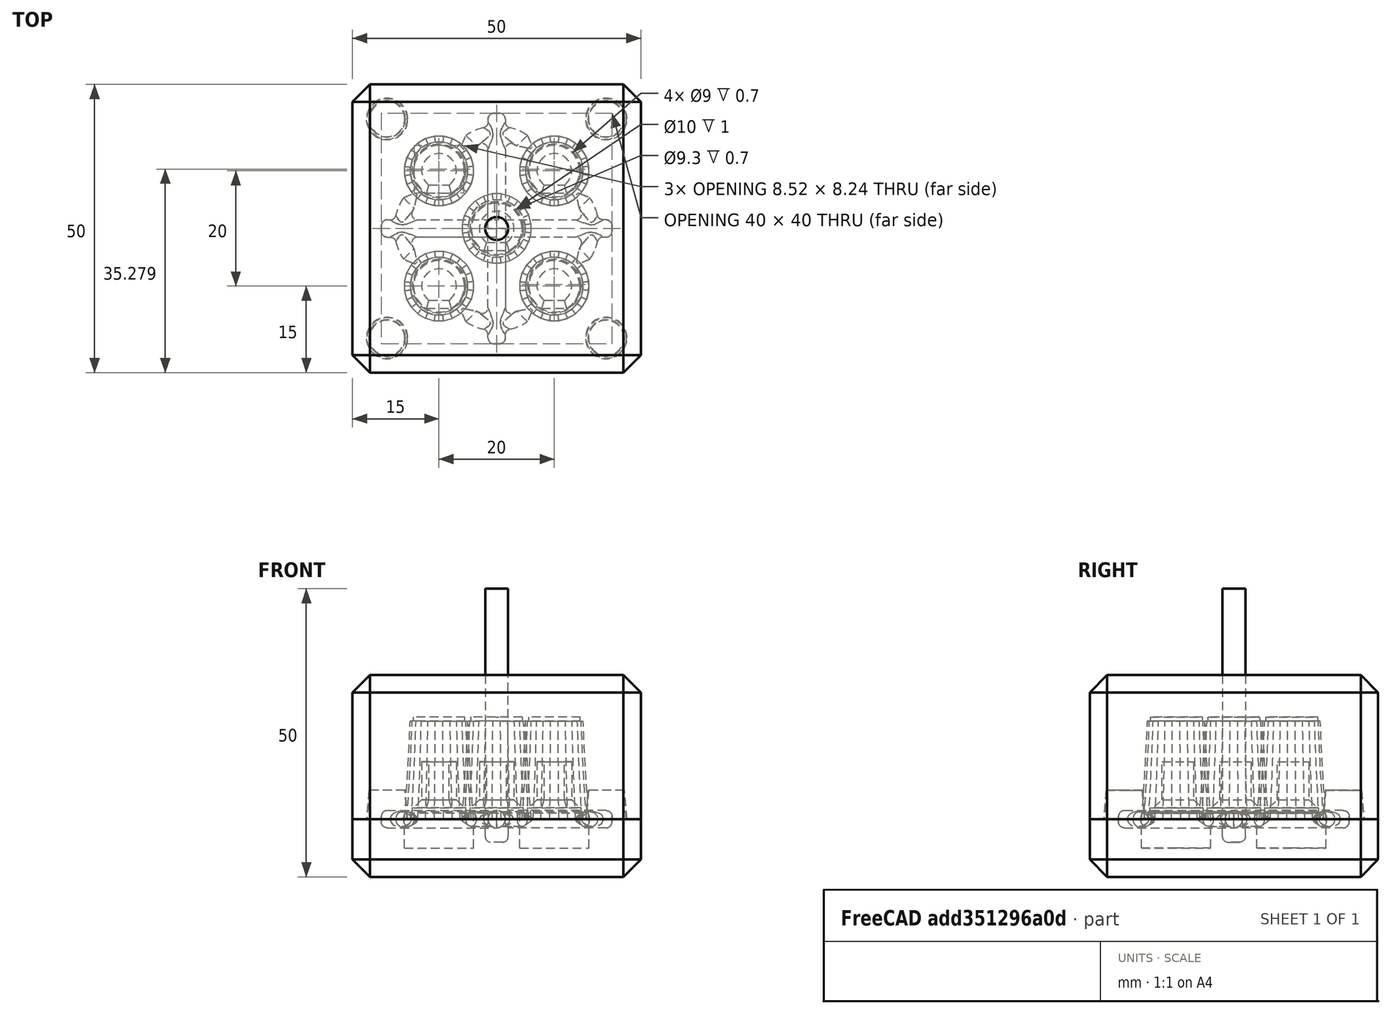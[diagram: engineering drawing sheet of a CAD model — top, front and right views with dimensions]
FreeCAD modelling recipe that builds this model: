
FCSTD DOCUMENT  (FreeCAD 0.19R23141 (Git))
Label: CapMould
License: All rights reserved
LicenseURL: http://en.wikipedia.org/wiki/All_rights_reserved
objects: Sketcher::SketchObject×45, PartDesign::Body×18, PartDesign::Pad×12, PartDesign::FeatureBase×7, PartDesign::Chamfer×6, PartDesign::Boolean×6, PartDesign::AdditiveLoft×5, PartDesign::Pocket×4, PartDesign::Fillet×3, PartDesign::Draft×2, PartDesign::AdditivePipe×1, PartDesign::Revolution×1
note: 144 computed .brp shape members not serialized (recipe doc carries the construction recipe); baked Part::Feature solids carry a one-line shape summary decoded from their .brp

FEATURE [Sketcher::SketchObject] Sketch
  MapMode = 5
  Support = -> [XY_Plane]
  sketch-geometry (25):
    g0: LineSegment StartX=-0.789915 StartY=6 StartZ=0 EndX=-2.31591 EndY=5.59111 EndZ=0
    g1: LineSegment StartX=-2.31591 StartY=5.59111 StartZ=0 EndX=-3.68409 EndY=4.80119 EndZ=0
    g2: LineSegment StartX=-3.68409 StartY=4.80119 StartZ=0 EndX=-4.80119 EndY=3.68409 EndZ=0
    g3: LineSegment StartX=-4.80119 StartY=3.68409 StartZ=0 EndX=-5.59111 EndY=2.31591 EndZ=0
    g4: LineSegment StartX=-5.59111 StartY=2.31591 StartZ=0 EndX=-6 EndY=0.789915 EndZ=0
    g5: LineSegment StartX=-6 StartY=0.789915 StartZ=0 EndX=-6 EndY=-0.789915 EndZ=0
    g6: LineSegment StartX=-6 StartY=-0.789915 StartZ=0 EndX=-5.59111 EndY=-2.31591 EndZ=0
    g7: LineSegment StartX=-5.59111 StartY=-2.31591 StartZ=0 EndX=-4.80119 EndY=-3.68409 EndZ=0
    g8: LineSegment StartX=-4.80119 StartY=-3.68409 StartZ=0 EndX=-3.68409 EndY=-4.80119 EndZ=0
    g9: LineSegment StartX=-3.68409 StartY=-4.80119 StartZ=0 EndX=-2.31591 EndY=-5.59111 EndZ=0
    g10: LineSegment StartX=-2.31591 StartY=-5.59111 StartZ=0 EndX=-0.789915 EndY=-6 EndZ=0
    g11: LineSegment StartX=-0.789915 StartY=-6 StartZ=0 EndX=0.789915 EndY=-6 EndZ=0
    g12: LineSegment StartX=0.789915 StartY=-6 StartZ=0 EndX=2.31591 EndY=-5.59111 EndZ=0
    g13: LineSegment StartX=2.31591 StartY=-5.59111 StartZ=0 EndX=3.68409 EndY=-4.80119 EndZ=0
    g14: LineSegment StartX=3.68409 StartY=-4.80119 StartZ=0 EndX=4.80119 EndY=-3.68409 EndZ=0
    g15: LineSegment StartX=4.80119 StartY=-3.68409 StartZ=0 EndX=5.59111 EndY=-2.31591 EndZ=0
    g16: LineSegment StartX=5.59111 StartY=-2.31591 StartZ=0 EndX=6 EndY=-0.789915 EndZ=0
    g17: LineSegment StartX=6 StartY=-0.789915 StartZ=0 EndX=6 EndY=0.789915 EndZ=0
    g18: LineSegment StartX=6 StartY=0.789915 StartZ=0 EndX=5.59111 EndY=2.31591 EndZ=0
    g19: LineSegment StartX=5.59111 StartY=2.31591 StartZ=0 EndX=4.80119 EndY=3.68409 EndZ=0
    g20: LineSegment StartX=4.80119 StartY=3.68409 StartZ=0 EndX=3.68409 EndY=4.80119 EndZ=0
    g21: LineSegment StartX=3.68409 StartY=4.80119 StartZ=0 EndX=2.31591 EndY=5.59111 EndZ=0
    g22: LineSegment StartX=2.31591 StartY=5.59111 StartZ=0 EndX=0.789915 EndY=6 EndZ=0
    g23: LineSegment StartX=0.789915 StartY=6 StartZ=0 EndX=-0.789915 EndY=6 EndZ=0
    g24: Circle [constr] CenterX=0 CenterY=0 CenterZ=0 NormalX=0 NormalY=0 NormalZ=1 AngleXU=0 Radius=6.05177
  constraints (52):
    c: Coincident(g0,g1)
    c: Coincident(g1,g2)
    c: Coincident(g2,g3)
    c: Coincident(g3,g4)
    c: Coincident(g4,g5)
    c: Coincident(g5,g6)
    c: Coincident(g6,g7)
    c: Coincident(g7,g8)
    c: Coincident(g8,g9)
    c: Coincident(g9,g10)
    c: Coincident(g10,g11)
    c: Coincident(g11,g12)
    c: Coincident(g12,g13)
    c: Coincident(g13,g14)
    c: Coincident(g14,g15)
    c: Coincident(g15,g16)
    c: Coincident(g16,g17)
    c: Coincident(g17,g18)
    c: Coincident(g18,g19)
    c: Coincident(g19,g20)
    c: Coincident(g20,g21)
    c: Coincident(g21,g22)
    c: Coincident(g22,g23)
    c: Coincident(g23,g0)
    c: Equal(g0, g1-g23) x23
    c: PointOnObject(g0,g24)
    c: PointOnObject(g1,g24)
    c: PointOnObject(g2,g24)
    c: PointOnObject(g3,g24)
    c: PointOnObject(g4,g24)
    c: PointOnObject(g5,g24)
    c: PointOnObject(g6,g24)
    c: PointOnObject(g7,g24)
    c: PointOnObject(g8,g24)
    c: PointOnObject(g9,g24)
    c: PointOnObject(g10,g24)
    c: PointOnObject(g11,g24)
    c: PointOnObject(g12,g24)
    c: PointOnObject(g13,g24)
    c: PointOnObject(g14,g24)
    c: PointOnObject(g15,g24)
    c: PointOnObject(g16,g24)
    c: PointOnObject(g17,g24)
    c: PointOnObject(g18,g24)
    c: PointOnObject(g19,g24)
    c: PointOnObject(g20,g24)
    c: PointOnObject(g21,g24)
    c: PointOnObject(g22,g24)
    c: PointOnObject(g23,g24)
    c: Coincident(g24,g-1)
    c: Horizontal(g23)
    c: DistanceX(g4,g17) = 12
FEATURE [Sketcher::SketchObject] Sketch001
  AttachmentOffset = pos=(0,0,7) rot=(0,0,1;0rad)
  MapMode = 5
  Placement = pos=(0,0,7) rot=(0,0,1;0rad)
  Support = -> [XY_Plane]
  sketch-geometry (25):
    g0: LineSegment StartX=-0.724089 StartY=5.5 StartZ=0 EndX=-2.12292 EndY=5.12518 EndZ=0
    g1: LineSegment StartX=-2.12292 StartY=5.12518 StartZ=0 EndX=-3.37708 EndY=4.4011 EndZ=0
    g2: LineSegment StartX=-3.37708 StartY=4.4011 StartZ=0 EndX=-4.4011 EndY=3.37708 EndZ=0
    g3: LineSegment StartX=-4.4011 StartY=3.37708 StartZ=0 EndX=-5.12518 EndY=2.12292 EndZ=0
    g4: LineSegment StartX=-5.12518 StartY=2.12292 StartZ=0 EndX=-5.5 EndY=0.724089 EndZ=0
    g5: LineSegment StartX=-5.5 StartY=0.724089 StartZ=0 EndX=-5.5 EndY=-0.724089 EndZ=0
    g6: LineSegment StartX=-5.5 StartY=-0.724089 StartZ=0 EndX=-5.12518 EndY=-2.12292 EndZ=0
    g7: LineSegment StartX=-5.12518 StartY=-2.12292 StartZ=0 EndX=-4.4011 EndY=-3.37708 EndZ=0
    g8: LineSegment StartX=-4.4011 StartY=-3.37708 StartZ=0 EndX=-3.37708 EndY=-4.4011 EndZ=0
    g9: LineSegment StartX=-3.37708 StartY=-4.4011 StartZ=0 EndX=-2.12292 EndY=-5.12518 EndZ=0
    g10: LineSegment StartX=-2.12292 StartY=-5.12518 StartZ=0 EndX=-0.724089 EndY=-5.5 EndZ=0
    g11: LineSegment StartX=-0.724089 StartY=-5.5 StartZ=0 EndX=0.724089 EndY=-5.5 EndZ=0
    g12: LineSegment StartX=0.724089 StartY=-5.5 StartZ=0 EndX=2.12292 EndY=-5.12518 EndZ=0
    g13: LineSegment StartX=2.12292 StartY=-5.12518 StartZ=0 EndX=3.37708 EndY=-4.4011 EndZ=0
    g14: LineSegment StartX=3.37708 StartY=-4.4011 StartZ=0 EndX=4.4011 EndY=-3.37708 EndZ=0
    g15: LineSegment StartX=4.4011 StartY=-3.37708 StartZ=0 EndX=5.12518 EndY=-2.12292 EndZ=0
    g16: LineSegment StartX=5.12518 StartY=-2.12292 StartZ=0 EndX=5.5 EndY=-0.724089 EndZ=0
    g17: LineSegment StartX=5.5 StartY=-0.724089 StartZ=0 EndX=5.5 EndY=0.724089 EndZ=0
    g18: LineSegment StartX=5.5 StartY=0.724089 StartZ=0 EndX=5.12518 EndY=2.12292 EndZ=0
    g19: LineSegment StartX=5.12518 StartY=2.12292 StartZ=0 EndX=4.4011 EndY=3.37708 EndZ=0
    g20: LineSegment StartX=4.4011 StartY=3.37708 StartZ=0 EndX=3.37708 EndY=4.4011 EndZ=0
    g21: LineSegment StartX=3.37708 StartY=4.4011 StartZ=0 EndX=2.12292 EndY=5.12518 EndZ=0
    g22: LineSegment StartX=2.12292 StartY=5.12518 StartZ=0 EndX=0.724089 EndY=5.5 EndZ=0
    g23: LineSegment StartX=0.724089 StartY=5.5 StartZ=0 EndX=-0.724089 EndY=5.5 EndZ=0
    g24: Circle [constr] CenterX=0 CenterY=0 CenterZ=0 NormalX=0 NormalY=0 NormalZ=1 AngleXU=0 Radius=5.54746
  constraints (52):
    c: Coincident(g0,g1)
    c: Coincident(g1,g2)
    c: Coincident(g2,g3)
    c: Coincident(g3,g4)
    c: Coincident(g4,g5)
    c: Coincident(g5,g6)
    c: Coincident(g6,g7)
    c: Coincident(g7,g8)
    c: Coincident(g8,g9)
    c: Coincident(g9,g10)
    c: Coincident(g10,g11)
    c: Coincident(g11,g12)
    c: Coincident(g12,g13)
    c: Coincident(g13,g14)
    c: Coincident(g14,g15)
    c: Coincident(g15,g16)
    c: Coincident(g16,g17)
    c: Coincident(g17,g18)
    c: Coincident(g18,g19)
    c: Coincident(g19,g20)
    c: Coincident(g20,g21)
    c: Coincident(g21,g22)
    c: Coincident(g22,g23)
    c: Coincident(g23,g0)
    c: Equal(g0, g1-g23) x23
    c: PointOnObject(g0,g24)
    c: PointOnObject(g1,g24)
    c: PointOnObject(g2,g24)
    c: PointOnObject(g3,g24)
    c: PointOnObject(g4,g24)
    c: PointOnObject(g5,g24)
    c: PointOnObject(g6,g24)
    c: PointOnObject(g7,g24)
    c: PointOnObject(g8,g24)
    c: PointOnObject(g9,g24)
    c: PointOnObject(g10,g24)
    c: PointOnObject(g11,g24)
    c: PointOnObject(g12,g24)
    c: PointOnObject(g13,g24)
    c: PointOnObject(g14,g24)
    c: PointOnObject(g15,g24)
    c: PointOnObject(g16,g24)
    c: PointOnObject(g17,g24)
    c: PointOnObject(g18,g24)
    c: PointOnObject(g19,g24)
    c: PointOnObject(g20,g24)
    c: PointOnObject(g21,g24)
    c: PointOnObject(g22,g24)
    c: PointOnObject(g23,g24)
    c: Coincident(g24,g-1)
    c: Horizontal(g23)
    c: DistanceX(g4,g17) = 11
FEATURE [Sketcher::SketchObject] Sketch002
  AttachmentOffset = pos=(0,0,17) rot=(0,0,1;0rad)
  MapMode = 5
  Placement = pos=(0,0,17) rot=(0,0,1;0rad)
  Support = -> [XY_Plane]
  sketch-geometry (25):
    g0: LineSegment StartX=-4.65926 StartY=1.92993 StartZ=0 EndX=-5 EndY=0.658262 EndZ=0
    g1: LineSegment StartX=-5 StartY=0.658262 StartZ=0 EndX=-5 EndY=-0.658262 EndZ=0
    g2: LineSegment StartX=-5 StartY=-0.658262 StartZ=0 EndX=-4.65926 EndY=-1.92993 EndZ=0
    g3: LineSegment StartX=-4.65926 StartY=-1.92993 StartZ=0 EndX=-4.001 EndY=-3.07007 EndZ=0
    g4: LineSegment StartX=-4.001 StartY=-3.07007 StartZ=0 EndX=-3.07007 EndY=-4.001 EndZ=0
    g5: LineSegment StartX=-3.07007 StartY=-4.001 StartZ=0 EndX=-1.92993 EndY=-4.65926 EndZ=0
    g6: LineSegment StartX=-1.92993 StartY=-4.65926 StartZ=0 EndX=-0.658262 EndY=-5 EndZ=0
    g7: LineSegment StartX=-0.658262 StartY=-5 StartZ=0 EndX=0.658262 EndY=-5 EndZ=0
    g8: LineSegment StartX=0.658262 StartY=-5 StartZ=0 EndX=1.92993 EndY=-4.65926 EndZ=0
    g9: LineSegment StartX=1.92993 StartY=-4.65926 StartZ=0 EndX=3.07007 EndY=-4.001 EndZ=0
    g10: LineSegment StartX=3.07007 StartY=-4.001 StartZ=0 EndX=4.001 EndY=-3.07007 EndZ=0
    g11: LineSegment StartX=4.001 StartY=-3.07007 StartZ=0 EndX=4.65926 EndY=-1.92993 EndZ=0
    g12: LineSegment StartX=4.65926 StartY=-1.92993 StartZ=0 EndX=5 EndY=-0.658262 EndZ=0
    g13: LineSegment StartX=5 StartY=-0.658262 StartZ=0 EndX=5 EndY=0.658262 EndZ=0
    g14: LineSegment StartX=5 StartY=0.658262 StartZ=0 EndX=4.65926 EndY=1.92993 EndZ=0
    g15: LineSegment StartX=4.65926 StartY=1.92993 StartZ=0 EndX=4.001 EndY=3.07007 EndZ=0
    g16: LineSegment StartX=4.001 StartY=3.07007 StartZ=0 EndX=3.07007 EndY=4.001 EndZ=0
    g17: LineSegment StartX=3.07007 StartY=4.001 StartZ=0 EndX=1.92993 EndY=4.65926 EndZ=0
    g18: LineSegment StartX=1.92993 StartY=4.65926 StartZ=0 EndX=0.658262 EndY=5 EndZ=0
    g19: LineSegment StartX=0.658262 StartY=5 StartZ=0 EndX=-0.658262 EndY=5 EndZ=0
    g20: LineSegment StartX=-0.658262 StartY=5 StartZ=0 EndX=-1.92993 EndY=4.65926 EndZ=0
    g21: LineSegment StartX=-1.92993 StartY=4.65926 StartZ=0 EndX=-3.07007 EndY=4.001 EndZ=0
    g22: LineSegment StartX=-3.07007 StartY=4.001 StartZ=0 EndX=-4.001 EndY=3.07007 EndZ=0
    g23: LineSegment StartX=-4.001 StartY=3.07007 StartZ=0 EndX=-4.65926 EndY=1.92993 EndZ=0
    g24: Circle [constr] CenterX=0 CenterY=0 CenterZ=0 NormalX=0 NormalY=0 NormalZ=1 AngleXU=0 Radius=5.04314
  constraints (52):
    c: Coincident(g0,g1)
    c: Coincident(g1,g2)
    c: Coincident(g2,g3)
    c: Coincident(g3,g4)
    c: Coincident(g4,g5)
    c: Coincident(g5,g6)
    c: Coincident(g6,g7)
    c: Coincident(g7,g8)
    c: Coincident(g8,g9)
    c: Coincident(g9,g10)
    c: Coincident(g10,g11)
    c: Coincident(g11,g12)
    c: Coincident(g12,g13)
    c: Coincident(g13,g14)
    c: Coincident(g14,g15)
    c: Coincident(g15,g16)
    c: Coincident(g16,g17)
    c: Coincident(g17,g18)
    c: Coincident(g18,g19)
    c: Coincident(g19,g20)
    c: Coincident(g20,g21)
    c: Coincident(g21,g22)
    c: Coincident(g22,g23)
    c: Coincident(g23,g0)
    c: Equal(g0, g1-g23) x23
    c: PointOnObject(g0,g24)
    c: PointOnObject(g1,g24)
    c: PointOnObject(g2,g24)
    c: PointOnObject(g3,g24)
    c: PointOnObject(g4,g24)
    c: PointOnObject(g5,g24)
    c: PointOnObject(g6,g24)
    c: PointOnObject(g7,g24)
    c: PointOnObject(g8,g24)
    c: PointOnObject(g9,g24)
    c: PointOnObject(g10,g24)
    c: PointOnObject(g11,g24)
    c: PointOnObject(g12,g24)
    c: PointOnObject(g13,g24)
    c: PointOnObject(g14,g24)
    c: PointOnObject(g15,g24)
    c: PointOnObject(g16,g24)
    c: PointOnObject(g17,g24)
    c: PointOnObject(g18,g24)
    c: PointOnObject(g19,g24)
    c: PointOnObject(g20,g24)
    c: PointOnObject(g21,g24)
    c: PointOnObject(g22,g24)
    c: PointOnObject(g23,g24)
    c: Coincident(g24,g-1)
    c: Horizontal(g19)
    c: DistanceX(g0,g13) = 10
FEATURE [PartDesign::AdditiveLoft] AdditiveLoft
  AllowMultiFace = false
  Closed = false
  Profile = -> Sketch
  Refine = true
  Ruled = false
  Sections = -> [Sketch001,Sketch002]
FEATURE [Sketcher::SketchObject] Sketch003
  MapMode = 5
  Placement = pos=(0,0,17) rot=(0,0,1;0rad)
  Support = -> [AdditiveLoft]
  sketch-geometry (1):
    g0: Circle CenterX=0 CenterY=0 CenterZ=0 NormalX=0 NormalY=0 NormalZ=1 AngleXU=0 Radius=4.5
  constraints (2):
    c: Coincident(g0,g-1)
    c: Radius(g0) = 4.5
FEATURE [PartDesign::Pad] Pad
  AllowMultiFace = false
  BaseFeature = -> AdditiveLoft
  Direction = (1,1,1)
  Length = 0.7
  Length2 = 100
  Profile = -> Sketch003
  Refine = true
  Type = 0
FEATURE [Sketcher::SketchObject] Sketch004
  AttachmentOffset = pos=(0,0,17.7) rot=(0,0,1;0rad)
  MapMode = 5
  Placement = pos=(0,0,17.7) rot=(0,0,1;0rad)
  Support = -> [XY_Plane001]
  sketch-geometry (10):
    g0: LineSegment StartX=-0.2 StartY=1.5 StartZ=0 EndX=0.2 EndY=1.5 EndZ=0
    g1: LineSegment StartX=0.4 StartY=1.7 StartZ=0 EndX=0.4 EndY=4.2 EndZ=0
    g2: LineSegment StartX=0.2 StartY=4.4 StartZ=0 EndX=-0.2 EndY=4.4 EndZ=0
    g3: LineSegment StartX=-0.4 StartY=4.2 StartZ=0 EndX=-0.4 EndY=1.7 EndZ=0
    g4: ArcOfCircle CenterX=-0.2 CenterY=1.7 CenterZ=0 NormalX=0 NormalY=0 NormalZ=1 AngleXU=0 Radius=0.2 StartAngle=3.14159 EndAngle=4.71239
    g5: ArcOfCircle CenterX=0.2 CenterY=1.7 CenterZ=0 NormalX=0 NormalY=0 NormalZ=1 AngleXU=0 Radius=0.2 StartAngle=4.71239 EndAngle=6.28319
    g6: ArcOfCircle CenterX=0.2 CenterY=4.2 CenterZ=0 NormalX=0 NormalY=0 NormalZ=1 AngleXU=0 Radius=0.2 StartAngle=1.4e-15 EndAngle=1.5708
    g7: ArcOfCircle CenterX=-0.2 CenterY=4.2 CenterZ=0 NormalX=0 NormalY=0 NormalZ=1 AngleXU=0 Radius=0.2 StartAngle=1.5708 EndAngle=3.14159
    g8: LineSegment [constr] StartX=-0.2 StartY=1.7 StartZ=0 EndX=0 EndY=0 EndZ=0
    g9: LineSegment [constr] StartX=0 StartY=0 StartZ=0 EndX=0.2 EndY=1.7 EndZ=0
  constraints (24):
    c: Horizontal(g0)
    c: Horizontal(g2)
    c: Vertical(g1)
    c: Vertical(g3)
    c: Tangent(g3,g4) = -1.5708
    c: Tangent(g0,g4) = -1.5708
    c: Tangent(g0,g5) = -1.5708
    c: Tangent(g1,g5) = -1.5708
    c: Tangent(g1,g6) = -1.5708
    c: Tangent(g2,g6) = -1.5708
    c: Tangent(g2,g7) = -1.5708
    c: Tangent(g3,g7) = -1.5708
    c: Radius(g7) = 0.2
    c: Equal(g7,g6)
    c: Equal(g7,g5)
    c: Equal(g7,g4)
    c: Coincident(g8,g4)
    c: Coincident(g8,g-1)
    c: Coincident(g9,g-1)
    c: Coincident(g9,g5)
    c: Equal(g9,g8)
    c: DistanceX(g3,g1) = 0.8
    c: DistanceY(g-1,g2) = 4.4
    c: DistanceY(g-1,g0) = 1.5
FEATURE [PartDesign::Pad] Pad001
  AllowMultiFace = false
  Direction = (1,1,1)
  Length = 0.02
  Length2 = 100
  Profile = -> Sketch004
  Refine = true
  Type = 0
FEATURE [PartDesign::Body] Body001  label="Indicator"
  Group = -> [Sketch004,Pad001]
  Origin = -> Origin001
  Tip = -> Pad001
FEATURE [Sketcher::SketchObject] Sketch005
  MapMode = 5
  Placement = pos=(0,0,0) rot=(1,0,0;3.14159rad)
  Support = -> [Pad]
  sketch-geometry (1):
    g0: Circle CenterX=0 CenterY=0 CenterZ=0 NormalX=0 NormalY=0 NormalZ=1 AngleXU=0 Radius=5
  constraints (2):
    c: Coincident(g0,g-1)
    c: Radius(g0) = 5
FEATURE [Sketcher::SketchObject] Sketch006
  MapMode = 5
  Placement = pos=(0,0,1) rot=(1,0,0;3.14159rad)
  sketch-geometry (1):
    g0: Circle CenterX=0 CenterY=0 CenterZ=0 NormalX=0 NormalY=0 NormalZ=1 AngleXU=0 Radius=4.65
  constraints (2):
    c: Coincident(g0,g-1)
    c: Radius(g0) = 4.65
FEATURE [Sketcher::SketchObject] Sketch007
  MapMode = 5
  Placement = pos=(0,0,2) rot=(1,0,0;3.14159rad)
  sketch-geometry (2):
    g0: ArcOfCircle CenterX=0 CenterY=0 CenterZ=0 NormalX=0 NormalY=0 NormalZ=1 AngleXU=0 Radius=3 StartAngle=2.19024 EndAngle=7.23453
    g1: LineSegment StartX=-1.74176 StartY=2.4426 StartZ=0 EndX=1.74176 EndY=2.4426 EndZ=0
  constraints (5):
    c: Coincident(g0,g-1)
    c: Coincident(g1,g0)
    c: Coincident(g1,g0)
    c: Horizontal(g1)
    c: Radius(g0) = 3
FEATURE [PartDesign::Body] Body  label="Outer"
  Group = -> [Sketch,Sketch001,Sketch002,AdditiveLoft,Sketch003,Pad,Sketch005,Sketch006,Sketch007]
  Origin = -> Origin
  Placement = pos=(-10,-10,0) rot=(0,0,1;0rad)
  Tip = -> Pad
FEATURE [Sketcher::SketchObject] Sketch008
  MapMode = 5
  Support = -> [XY_Plane002]
  sketch-geometry (5):
    g0: LineSegment StartX=-25 StartY=25 StartZ=0 EndX=-25 EndY=-25 EndZ=0
    g1: LineSegment StartX=-25 StartY=-25 StartZ=0 EndX=25 EndY=-25 EndZ=0
    g2: LineSegment StartX=25 StartY=-25 StartZ=0 EndX=25 EndY=25 EndZ=0
    g3: LineSegment StartX=25 StartY=25 StartZ=0 EndX=-25 EndY=25 EndZ=0
    g4: Circle [constr] CenterX=0 CenterY=0 CenterZ=0 NormalX=0 NormalY=0 NormalZ=1 AngleXU=0 Radius=35.3553
  constraints (14):
    c: Coincident(g0,g1)
    c: Coincident(g1,g2)
    c: Coincident(g2,g3)
    c: Coincident(g3,g0)
    c: Equal(g0,g1)
    c: Equal(g0,g2)
    c: Equal(g0,g3)
    c: PointOnObject(g0,g4)
    c: PointOnObject(g1,g4)
    c: PointOnObject(g2,g4)
    c: PointOnObject(g3,g4)
    c: Coincident(g4,g-1)
    c: Horizontal(g3)
    c: DistanceX(g3,g3) = 50
FEATURE [PartDesign::Pad] Pad002
  Direction = (1,1,1)
  Length = 25
  Length2 = 100
  Profile = -> Sketch008
  Type = 0
FEATURE [Sketcher::SketchObject] Sketch009
  AttachmentOffset = pos=(0,0,17) rot=(0,0,1;0rad)
  MapMode = 5
  Placement = pos=(0,0,17) rot=(0,0,1;0rad)
  Support = -> [XY_Plane003]
  sketch-geometry (25):
    g0: LineSegment StartX=-4.65926 StartY=1.92993 StartZ=0 EndX=-5 EndY=0.658262 EndZ=0
    g1: LineSegment StartX=-5 StartY=0.658262 StartZ=0 EndX=-5 EndY=-0.658262 EndZ=0
    g2: LineSegment StartX=-5 StartY=-0.658262 StartZ=0 EndX=-4.65926 EndY=-1.92993 EndZ=0
    g3: LineSegment StartX=-4.65926 StartY=-1.92993 StartZ=0 EndX=-4.001 EndY=-3.07007 EndZ=0
    g4: LineSegment StartX=-4.001 StartY=-3.07007 StartZ=0 EndX=-3.07007 EndY=-4.001 EndZ=0
    g5: LineSegment StartX=-3.07007 StartY=-4.001 StartZ=0 EndX=-1.92993 EndY=-4.65926 EndZ=0
    g6: LineSegment StartX=-1.92993 StartY=-4.65926 StartZ=0 EndX=-0.658262 EndY=-5 EndZ=0
    g7: LineSegment StartX=-0.658262 StartY=-5 StartZ=0 EndX=0.658262 EndY=-5 EndZ=0
    g8: LineSegment StartX=0.658262 StartY=-5 StartZ=0 EndX=1.92993 EndY=-4.65926 EndZ=0
    g9: LineSegment StartX=1.92993 StartY=-4.65926 StartZ=0 EndX=3.07007 EndY=-4.001 EndZ=0
    g10: LineSegment StartX=3.07007 StartY=-4.001 StartZ=0 EndX=4.001 EndY=-3.07007 EndZ=0
    g11: LineSegment StartX=4.001 StartY=-3.07007 StartZ=0 EndX=4.65926 EndY=-1.92993 EndZ=0
    g12: LineSegment StartX=4.65926 StartY=-1.92993 StartZ=0 EndX=5 EndY=-0.658262 EndZ=0
    g13: LineSegment StartX=5 StartY=-0.658262 StartZ=0 EndX=5 EndY=0.658262 EndZ=0
    g14: LineSegment StartX=5 StartY=0.658262 StartZ=0 EndX=4.65926 EndY=1.92993 EndZ=0
    g15: LineSegment StartX=4.65926 StartY=1.92993 StartZ=0 EndX=4.001 EndY=3.07007 EndZ=0
    g16: LineSegment StartX=4.001 StartY=3.07007 StartZ=0 EndX=3.07007 EndY=4.001 EndZ=0
    g17: LineSegment StartX=3.07007 StartY=4.001 StartZ=0 EndX=1.92993 EndY=4.65926 EndZ=0
    g18: LineSegment StartX=1.92993 StartY=4.65926 StartZ=0 EndX=0.658262 EndY=5 EndZ=0
    g19: LineSegment StartX=0.658262 StartY=5 StartZ=0 EndX=-0.658262 EndY=5 EndZ=0
    g20: LineSegment StartX=-0.658262 StartY=5 StartZ=0 EndX=-1.92993 EndY=4.65926 EndZ=0
    g21: LineSegment StartX=-1.92993 StartY=4.65926 StartZ=0 EndX=-3.07007 EndY=4.001 EndZ=0
    g22: LineSegment StartX=-3.07007 StartY=4.001 StartZ=0 EndX=-4.001 EndY=3.07007 EndZ=0
    g23: LineSegment StartX=-4.001 StartY=3.07007 StartZ=0 EndX=-4.65926 EndY=1.92993 EndZ=0
    g24: Circle [constr] CenterX=0 CenterY=0 CenterZ=0 NormalX=0 NormalY=0 NormalZ=1 AngleXU=0 Radius=5.04314
  constraints (52):
    c: Coincident(g0,g1)
    c: Coincident(g1,g2)
    c: Coincident(g2,g3)
    c: Coincident(g3,g4)
    c: Coincident(g4,g5)
    c: Coincident(g5,g6)
    c: Coincident(g6,g7)
    c: Coincident(g7,g8)
    c: Coincident(g8,g9)
    c: Coincident(g9,g10)
    c: Coincident(g10,g11)
    c: Coincident(g11,g12)
    c: Coincident(g12,g13)
    c: Coincident(g13,g14)
    c: Coincident(g14,g15)
    c: Coincident(g15,g16)
    c: Coincident(g16,g17)
    c: Coincident(g17,g18)
    c: Coincident(g18,g19)
    c: Coincident(g19,g20)
    c: Coincident(g20,g21)
    c: Coincident(g21,g22)
    c: Coincident(g22,g23)
    c: Coincident(g23,g0)
    c: Equal(g0, g1-g23) x23
    c: PointOnObject(g0,g24)
    c: PointOnObject(g1,g24)
    c: PointOnObject(g2,g24)
    c: PointOnObject(g3,g24)
    c: PointOnObject(g4,g24)
    c: PointOnObject(g5,g24)
    c: PointOnObject(g6,g24)
    c: PointOnObject(g7,g24)
    c: PointOnObject(g8,g24)
    c: PointOnObject(g9,g24)
    c: PointOnObject(g10,g24)
    c: PointOnObject(g11,g24)
    c: PointOnObject(g12,g24)
    c: PointOnObject(g13,g24)
    c: PointOnObject(g14,g24)
    c: PointOnObject(g15,g24)
    c: PointOnObject(g16,g24)
    c: PointOnObject(g17,g24)
    c: PointOnObject(g18,g24)
    c: PointOnObject(g19,g24)
    c: PointOnObject(g20,g24)
    c: PointOnObject(g21,g24)
    c: PointOnObject(g22,g24)
    c: PointOnObject(g23,g24)
    c: Coincident(g24,g-1)
    c: Horizontal(g19)
    c: DistanceX(g0,g13) = 10
FEATURE [Sketcher::SketchObject] Sketch011
  MapMode = 5
  Support = -> [XY_Plane003]
  sketch-geometry (25):
    g0: LineSegment StartX=-0.789915 StartY=6 StartZ=0 EndX=-2.31591 EndY=5.59111 EndZ=0
    g1: LineSegment StartX=-2.31591 StartY=5.59111 StartZ=0 EndX=-3.68409 EndY=4.80119 EndZ=0
    g2: LineSegment StartX=-3.68409 StartY=4.80119 StartZ=0 EndX=-4.80119 EndY=3.68409 EndZ=0
    g3: LineSegment StartX=-4.80119 StartY=3.68409 StartZ=0 EndX=-5.59111 EndY=2.31591 EndZ=0
    g4: LineSegment StartX=-5.59111 StartY=2.31591 StartZ=0 EndX=-6 EndY=0.789915 EndZ=0
    g5: LineSegment StartX=-6 StartY=0.789915 StartZ=0 EndX=-6 EndY=-0.789915 EndZ=0
    g6: LineSegment StartX=-6 StartY=-0.789915 StartZ=0 EndX=-5.59111 EndY=-2.31591 EndZ=0
    g7: LineSegment StartX=-5.59111 StartY=-2.31591 StartZ=0 EndX=-4.80119 EndY=-3.68409 EndZ=0
    g8: LineSegment StartX=-4.80119 StartY=-3.68409 StartZ=0 EndX=-3.68409 EndY=-4.80119 EndZ=0
    g9: LineSegment StartX=-3.68409 StartY=-4.80119 StartZ=0 EndX=-2.31591 EndY=-5.59111 EndZ=0
    g10: LineSegment StartX=-2.31591 StartY=-5.59111 StartZ=0 EndX=-0.789915 EndY=-6 EndZ=0
    g11: LineSegment StartX=-0.789915 StartY=-6 StartZ=0 EndX=0.789915 EndY=-6 EndZ=0
    g12: LineSegment StartX=0.789915 StartY=-6 StartZ=0 EndX=2.31591 EndY=-5.59111 EndZ=0
    g13: LineSegment StartX=2.31591 StartY=-5.59111 StartZ=0 EndX=3.68409 EndY=-4.80119 EndZ=0
    g14: LineSegment StartX=3.68409 StartY=-4.80119 StartZ=0 EndX=4.80119 EndY=-3.68409 EndZ=0
    g15: LineSegment StartX=4.80119 StartY=-3.68409 StartZ=0 EndX=5.59111 EndY=-2.31591 EndZ=0
    g16: LineSegment StartX=5.59111 StartY=-2.31591 StartZ=0 EndX=6 EndY=-0.789915 EndZ=0
    g17: LineSegment StartX=6 StartY=-0.789915 StartZ=0 EndX=6 EndY=0.789915 EndZ=0
    g18: LineSegment StartX=6 StartY=0.789915 StartZ=0 EndX=5.59111 EndY=2.31591 EndZ=0
    g19: LineSegment StartX=5.59111 StartY=2.31591 StartZ=0 EndX=4.80119 EndY=3.68409 EndZ=0
    g20: LineSegment StartX=4.80119 StartY=3.68409 StartZ=0 EndX=3.68409 EndY=4.80119 EndZ=0
    g21: LineSegment StartX=3.68409 StartY=4.80119 StartZ=0 EndX=2.31591 EndY=5.59111 EndZ=0
    g22: LineSegment StartX=2.31591 StartY=5.59111 StartZ=0 EndX=0.789915 EndY=6 EndZ=0
    g23: LineSegment StartX=0.789915 StartY=6 StartZ=0 EndX=-0.789915 EndY=6 EndZ=0
    g24: Circle [constr] CenterX=0 CenterY=0 CenterZ=0 NormalX=0 NormalY=0 NormalZ=1 AngleXU=0 Radius=6.05177
  constraints (52):
    c: Coincident(g0,g1)
    c: Coincident(g1,g2)
    c: Coincident(g2,g3)
    c: Coincident(g3,g4)
    c: Coincident(g4,g5)
    c: Coincident(g5,g6)
    c: Coincident(g6,g7)
    c: Coincident(g7,g8)
    c: Coincident(g8,g9)
    c: Coincident(g9,g10)
    c: Coincident(g10,g11)
    c: Coincident(g11,g12)
    c: Coincident(g12,g13)
    c: Coincident(g13,g14)
    c: Coincident(g14,g15)
    c: Coincident(g15,g16)
    c: Coincident(g16,g17)
    c: Coincident(g17,g18)
    c: Coincident(g18,g19)
    c: Coincident(g19,g20)
    c: Coincident(g20,g21)
    c: Coincident(g21,g22)
    c: Coincident(g22,g23)
    c: Coincident(g23,g0)
    c: Equal(g0, g1-g23) x23
    c: PointOnObject(g0,g24)
    c: PointOnObject(g1,g24)
    c: PointOnObject(g2,g24)
    c: PointOnObject(g3,g24)
    c: PointOnObject(g4,g24)
    c: PointOnObject(g5,g24)
    c: PointOnObject(g6,g24)
    c: PointOnObject(g7,g24)
    c: PointOnObject(g8,g24)
    c: PointOnObject(g9,g24)
    c: PointOnObject(g10,g24)
    c: PointOnObject(g11,g24)
    c: PointOnObject(g12,g24)
    c: PointOnObject(g13,g24)
    c: PointOnObject(g14,g24)
    c: PointOnObject(g15,g24)
    c: PointOnObject(g16,g24)
    c: PointOnObject(g17,g24)
    c: PointOnObject(g18,g24)
    c: PointOnObject(g19,g24)
    c: PointOnObject(g20,g24)
    c: PointOnObject(g21,g24)
    c: PointOnObject(g22,g24)
    c: PointOnObject(g23,g24)
    c: Coincident(g24,g-1)
    c: Horizontal(g23)
    c: DistanceX(g4,g17) = 12
FEATURE [Sketcher::SketchObject] Sketch012
  AttachmentOffset = pos=(0,0,7) rot=(0,0,1;0rad)
  MapMode = 5
  Placement = pos=(0,0,7) rot=(0,0,1;0rad)
  Support = -> [XY_Plane003]
  sketch-geometry (25):
    g0: LineSegment StartX=-0.724089 StartY=5.5 StartZ=0 EndX=-2.12292 EndY=5.12518 EndZ=0
    g1: LineSegment StartX=-2.12292 StartY=5.12518 StartZ=0 EndX=-3.37708 EndY=4.4011 EndZ=0
    g2: LineSegment StartX=-3.37708 StartY=4.4011 StartZ=0 EndX=-4.4011 EndY=3.37708 EndZ=0
    g3: LineSegment StartX=-4.4011 StartY=3.37708 StartZ=0 EndX=-5.12518 EndY=2.12292 EndZ=0
    g4: LineSegment StartX=-5.12518 StartY=2.12292 StartZ=0 EndX=-5.5 EndY=0.724089 EndZ=0
    g5: LineSegment StartX=-5.5 StartY=0.724089 StartZ=0 EndX=-5.5 EndY=-0.724089 EndZ=0
    g6: LineSegment StartX=-5.5 StartY=-0.724089 StartZ=0 EndX=-5.12518 EndY=-2.12292 EndZ=0
    g7: LineSegment StartX=-5.12518 StartY=-2.12292 StartZ=0 EndX=-4.4011 EndY=-3.37708 EndZ=0
    g8: LineSegment StartX=-4.4011 StartY=-3.37708 StartZ=0 EndX=-3.37708 EndY=-4.4011 EndZ=0
    g9: LineSegment StartX=-3.37708 StartY=-4.4011 StartZ=0 EndX=-2.12292 EndY=-5.12518 EndZ=0
    g10: LineSegment StartX=-2.12292 StartY=-5.12518 StartZ=0 EndX=-0.724089 EndY=-5.5 EndZ=0
    g11: LineSegment StartX=-0.724089 StartY=-5.5 StartZ=0 EndX=0.724089 EndY=-5.5 EndZ=0
    g12: LineSegment StartX=0.724089 StartY=-5.5 StartZ=0 EndX=2.12292 EndY=-5.12518 EndZ=0
    g13: LineSegment StartX=2.12292 StartY=-5.12518 StartZ=0 EndX=3.37708 EndY=-4.4011 EndZ=0
    g14: LineSegment StartX=3.37708 StartY=-4.4011 StartZ=0 EndX=4.4011 EndY=-3.37708 EndZ=0
    g15: LineSegment StartX=4.4011 StartY=-3.37708 StartZ=0 EndX=5.12518 EndY=-2.12292 EndZ=0
    g16: LineSegment StartX=5.12518 StartY=-2.12292 StartZ=0 EndX=5.5 EndY=-0.724089 EndZ=0
    g17: LineSegment StartX=5.5 StartY=-0.724089 StartZ=0 EndX=5.5 EndY=0.724089 EndZ=0
    g18: LineSegment StartX=5.5 StartY=0.724089 StartZ=0 EndX=5.12518 EndY=2.12292 EndZ=0
    g19: LineSegment StartX=5.12518 StartY=2.12292 StartZ=0 EndX=4.4011 EndY=3.37708 EndZ=0
    g20: LineSegment StartX=4.4011 StartY=3.37708 StartZ=0 EndX=3.37708 EndY=4.4011 EndZ=0
    g21: LineSegment StartX=3.37708 StartY=4.4011 StartZ=0 EndX=2.12292 EndY=5.12518 EndZ=0
    g22: LineSegment StartX=2.12292 StartY=5.12518 StartZ=0 EndX=0.724089 EndY=5.5 EndZ=0
    g23: LineSegment StartX=0.724089 StartY=5.5 StartZ=0 EndX=-0.724089 EndY=5.5 EndZ=0
    g24: Circle [constr] CenterX=0 CenterY=0 CenterZ=0 NormalX=0 NormalY=0 NormalZ=1 AngleXU=0 Radius=5.54746
  constraints (52):
    c: Coincident(g0,g1)
    c: Coincident(g1,g2)
    c: Coincident(g2,g3)
    c: Coincident(g3,g4)
    c: Coincident(g4,g5)
    c: Coincident(g5,g6)
    c: Coincident(g6,g7)
    c: Coincident(g7,g8)
    c: Coincident(g8,g9)
    c: Coincident(g9,g10)
    c: Coincident(g10,g11)
    c: Coincident(g11,g12)
    c: Coincident(g12,g13)
    c: Coincident(g13,g14)
    c: Coincident(g14,g15)
    c: Coincident(g15,g16)
    c: Coincident(g16,g17)
    c: Coincident(g17,g18)
    c: Coincident(g18,g19)
    c: Coincident(g19,g20)
    c: Coincident(g20,g21)
    c: Coincident(g21,g22)
    c: Coincident(g22,g23)
    c: Coincident(g23,g0)
    c: Equal(g0, g1-g23) x23
    c: PointOnObject(g0,g24)
    c: PointOnObject(g1,g24)
    c: PointOnObject(g2,g24)
    c: PointOnObject(g3,g24)
    c: PointOnObject(g4,g24)
    c: PointOnObject(g5,g24)
    c: PointOnObject(g6,g24)
    c: PointOnObject(g7,g24)
    c: PointOnObject(g8,g24)
    c: PointOnObject(g9,g24)
    c: PointOnObject(g10,g24)
    c: PointOnObject(g11,g24)
    c: PointOnObject(g12,g24)
    c: PointOnObject(g13,g24)
    c: PointOnObject(g14,g24)
    c: PointOnObject(g15,g24)
    c: PointOnObject(g16,g24)
    c: PointOnObject(g17,g24)
    c: PointOnObject(g18,g24)
    c: PointOnObject(g19,g24)
    c: PointOnObject(g20,g24)
    c: PointOnObject(g21,g24)
    c: PointOnObject(g22,g24)
    c: PointOnObject(g23,g24)
    c: Coincident(g24,g-1)
    c: Horizontal(g23)
    c: DistanceX(g4,g17) = 11
FEATURE [PartDesign::AdditiveLoft] AdditiveLoft001
  AllowMultiFace = false
  Closed = false
  Profile = -> Sketch011
  Refine = true
  Ruled = false
  Sections = -> [Sketch012,Sketch009]
FEATURE [Sketcher::SketchObject] Sketch010
  MapMode = 5
  Placement = pos=(0,0,17) rot=(0,0,1;0rad)
  Support = -> [AdditiveLoft001]
  sketch-geometry (1):
    g0: Circle CenterX=0 CenterY=0 CenterZ=0 NormalX=0 NormalY=0 NormalZ=1 AngleXU=0 Radius=4.5
  constraints (2):
    c: Coincident(g0,g-1)
    c: Radius(g0) = 4.5
FEATURE [PartDesign::Pad] Pad003
  AllowMultiFace = false
  BaseFeature = -> AdditiveLoft001
  Direction = (1,1,1)
  Length = 0.7
  Length2 = 100
  Profile = -> Sketch010
  Refine = true
  Type = 0
FEATURE [Sketcher::SketchObject] Sketch013
  MapMode = 5
  Placement = pos=(0,0,0) rot=(1,0,0;3.14159rad)
  Support = -> [Pad003]
  sketch-geometry (1):
    g0: Circle CenterX=0 CenterY=0 CenterZ=0 NormalX=0 NormalY=0 NormalZ=1 AngleXU=0 Radius=5
  constraints (2):
    c: Coincident(g0,g-1)
    c: Radius(g0) = 5
FEATURE [PartDesign::Pocket] Pocket003
  AllowMultiFace = false
  BaseFeature = -> Pad003
  Length = 1
  Length2 = 100
  Profile = -> Sketch013
  Refine = true
  Type = 0
FEATURE [Sketcher::SketchObject] Sketch014
  MapMode = 5
  Placement = pos=(0,0,1) rot=(1,0,0;3.14159rad)
  Support = -> [Pocket003]
  sketch-geometry (1):
    g0: Circle CenterX=0 CenterY=0 CenterZ=0 NormalX=0 NormalY=0 NormalZ=1 AngleXU=0 Radius=4.65
  constraints (2):
    c: Coincident(g0,g-1)
    c: Radius(g0) = 4.65
FEATURE [PartDesign::Pocket] Pocket004
  AllowMultiFace = false
  BaseFeature = -> Pocket003
  Length = 1
  Length2 = 100
  Profile = -> Sketch014
  Refine = true
  Type = 0
FEATURE [Sketcher::SketchObject] Sketch015
  MapMode = 5
  Placement = pos=(0,0,2) rot=(1,0,0;3.14159rad)
  Support = -> [Pocket004]
  sketch-geometry (2):
    g0: ArcOfCircle CenterX=0 CenterY=0 CenterZ=0 NormalX=0 NormalY=0 NormalZ=1 AngleXU=0 Radius=3 StartAngle=2.19024 EndAngle=7.23453
    g1: LineSegment StartX=-1.74176 StartY=2.4426 StartZ=0 EndX=1.74176 EndY=2.4426 EndZ=0
  constraints (5):
    c: Coincident(g0,g-1)
    c: Coincident(g1,g0)
    c: Coincident(g1,g0)
    c: Horizontal(g1)
    c: Radius(g0) = 3
FEATURE [PartDesign::Pocket] Pocket005
  AllowMultiFace = false
  BaseFeature = -> Pocket004
  Length = 8
  Length2 = 100
  Profile = -> Sketch015
  Refine = true
  Type = 0
FEATURE [PartDesign::Chamfer] Chamfer002
  Angle = 45
  Base = -> Pocket005 [Edge82,Edge83]
  BaseFeature = -> Pocket005
  ChamferType = 0
  FlipDirection = false
  Size = 1.4
  Size2 = 1
  SupportTransform = false
FEATURE [PartDesign::Chamfer] Chamfer003
  Angle = 45
  Base = -> Chamfer002 [Edge8]
  BaseFeature = -> Chamfer002
  ChamferType = 0
  FlipDirection = false
  Size = 0.3
  Size2 = 1
  SupportTransform = false
FEATURE [PartDesign::Fillet] Fillet001
  Base = -> Chamfer003 [Edge93,Face36]
  BaseFeature = -> Chamfer003
  Radius = 0.1
  SupportTransform = false
FEATURE [PartDesign::Body] Body003  label="Inner"
  Group = -> [Sketch011,Sketch012,Sketch009,AdditiveLoft001,Sketch010,Pad003,Sketch013,Pocket003,Sketch014,Pocket004,Sketch015,Pocket005,Chamfer002,Chamfer003,Fillet001]
  Origin = -> Origin003
  Tip = -> Fillet001
FEATURE [Sketcher::SketchObject] Sketch016
  AttachmentOffset = pos=(0,0,17) rot=(0,0,1;0rad)
  MapMode = 5
  Placement = pos=(0,0,17) rot=(0,0,1;0rad)
  Support = -> [XY_Plane004]
  sketch-geometry (25):
    g0: LineSegment StartX=-4.65926 StartY=1.92993 StartZ=0 EndX=-5 EndY=0.658262 EndZ=0
    g1: LineSegment StartX=-5 StartY=0.658262 StartZ=0 EndX=-5 EndY=-0.658262 EndZ=0
    g2: LineSegment StartX=-5 StartY=-0.658262 StartZ=0 EndX=-4.65926 EndY=-1.92993 EndZ=0
    g3: LineSegment StartX=-4.65926 StartY=-1.92993 StartZ=0 EndX=-4.001 EndY=-3.07007 EndZ=0
    g4: LineSegment StartX=-4.001 StartY=-3.07007 StartZ=0 EndX=-3.07007 EndY=-4.001 EndZ=0
    g5: LineSegment StartX=-3.07007 StartY=-4.001 StartZ=0 EndX=-1.92993 EndY=-4.65926 EndZ=0
    g6: LineSegment StartX=-1.92993 StartY=-4.65926 StartZ=0 EndX=-0.658262 EndY=-5 EndZ=0
    g7: LineSegment StartX=-0.658262 StartY=-5 StartZ=0 EndX=0.658262 EndY=-5 EndZ=0
    g8: LineSegment StartX=0.658262 StartY=-5 StartZ=0 EndX=1.92993 EndY=-4.65926 EndZ=0
    g9: LineSegment StartX=1.92993 StartY=-4.65926 StartZ=0 EndX=3.07007 EndY=-4.001 EndZ=0
    g10: LineSegment StartX=3.07007 StartY=-4.001 StartZ=0 EndX=4.001 EndY=-3.07007 EndZ=0
    g11: LineSegment StartX=4.001 StartY=-3.07007 StartZ=0 EndX=4.65926 EndY=-1.92993 EndZ=0
    g12: LineSegment StartX=4.65926 StartY=-1.92993 StartZ=0 EndX=5 EndY=-0.658262 EndZ=0
    g13: LineSegment StartX=5 StartY=-0.658262 StartZ=0 EndX=5 EndY=0.658262 EndZ=0
    g14: LineSegment StartX=5 StartY=0.658262 StartZ=0 EndX=4.65926 EndY=1.92993 EndZ=0
    g15: LineSegment StartX=4.65926 StartY=1.92993 StartZ=0 EndX=4.001 EndY=3.07007 EndZ=0
    g16: LineSegment StartX=4.001 StartY=3.07007 StartZ=0 EndX=3.07007 EndY=4.001 EndZ=0
    g17: LineSegment StartX=3.07007 StartY=4.001 StartZ=0 EndX=1.92993 EndY=4.65926 EndZ=0
    g18: LineSegment StartX=1.92993 StartY=4.65926 StartZ=0 EndX=0.658262 EndY=5 EndZ=0
    g19: LineSegment StartX=0.658262 StartY=5 StartZ=0 EndX=-0.658262 EndY=5 EndZ=0
    g20: LineSegment StartX=-0.658262 StartY=5 StartZ=0 EndX=-1.92993 EndY=4.65926 EndZ=0
    g21: LineSegment StartX=-1.92993 StartY=4.65926 StartZ=0 EndX=-3.07007 EndY=4.001 EndZ=0
    g22: LineSegment StartX=-3.07007 StartY=4.001 StartZ=0 EndX=-4.001 EndY=3.07007 EndZ=0
    g23: LineSegment StartX=-4.001 StartY=3.07007 StartZ=0 EndX=-4.65926 EndY=1.92993 EndZ=0
    g24: Circle [constr] CenterX=0 CenterY=0 CenterZ=0 NormalX=0 NormalY=0 NormalZ=1 AngleXU=0 Radius=5.04314
  constraints (52):
    c: Coincident(g0,g1)
    c: Coincident(g1,g2)
    c: Coincident(g2,g3)
    c: Coincident(g3,g4)
    c: Coincident(g4,g5)
    c: Coincident(g5,g6)
    c: Coincident(g6,g7)
    c: Coincident(g7,g8)
    c: Coincident(g8,g9)
    c: Coincident(g9,g10)
    c: Coincident(g10,g11)
    c: Coincident(g11,g12)
    c: Coincident(g12,g13)
    c: Coincident(g13,g14)
    c: Coincident(g14,g15)
    c: Coincident(g15,g16)
    c: Coincident(g16,g17)
    c: Coincident(g17,g18)
    c: Coincident(g18,g19)
    c: Coincident(g19,g20)
    c: Coincident(g20,g21)
    c: Coincident(g21,g22)
    c: Coincident(g22,g23)
    c: Coincident(g23,g0)
    c: Equal(g0, g1-g23) x23
    c: PointOnObject(g0,g24)
    c: PointOnObject(g1,g24)
    c: PointOnObject(g2,g24)
    c: PointOnObject(g3,g24)
    c: PointOnObject(g4,g24)
    c: PointOnObject(g5,g24)
    c: PointOnObject(g6,g24)
    c: PointOnObject(g7,g24)
    c: PointOnObject(g8,g24)
    c: PointOnObject(g9,g24)
    c: PointOnObject(g10,g24)
    c: PointOnObject(g11,g24)
    c: PointOnObject(g12,g24)
    c: PointOnObject(g13,g24)
    c: PointOnObject(g14,g24)
    c: PointOnObject(g15,g24)
    c: PointOnObject(g16,g24)
    c: PointOnObject(g17,g24)
    c: PointOnObject(g18,g24)
    c: PointOnObject(g19,g24)
    c: PointOnObject(g20,g24)
    c: PointOnObject(g21,g24)
    c: PointOnObject(g22,g24)
    c: PointOnObject(g23,g24)
    c: Coincident(g24,g-1)
    c: Horizontal(g19)
    c: DistanceX(g0,g13) = 10
FEATURE [Sketcher::SketchObject] Sketch018
  MapMode = 5
  Support = -> [XY_Plane004]
  sketch-geometry (25):
    g0: LineSegment StartX=-0.789915 StartY=6 StartZ=0 EndX=-2.31591 EndY=5.59111 EndZ=0
    g1: LineSegment StartX=-2.31591 StartY=5.59111 StartZ=0 EndX=-3.68409 EndY=4.80119 EndZ=0
    g2: LineSegment StartX=-3.68409 StartY=4.80119 StartZ=0 EndX=-4.80119 EndY=3.68409 EndZ=0
    g3: LineSegment StartX=-4.80119 StartY=3.68409 StartZ=0 EndX=-5.59111 EndY=2.31591 EndZ=0
    g4: LineSegment StartX=-5.59111 StartY=2.31591 StartZ=0 EndX=-6 EndY=0.789915 EndZ=0
    g5: LineSegment StartX=-6 StartY=0.789915 StartZ=0 EndX=-6 EndY=-0.789915 EndZ=0
    g6: LineSegment StartX=-6 StartY=-0.789915 StartZ=0 EndX=-5.59111 EndY=-2.31591 EndZ=0
    g7: LineSegment StartX=-5.59111 StartY=-2.31591 StartZ=0 EndX=-4.80119 EndY=-3.68409 EndZ=0
    g8: LineSegment StartX=-4.80119 StartY=-3.68409 StartZ=0 EndX=-3.68409 EndY=-4.80119 EndZ=0
    g9: LineSegment StartX=-3.68409 StartY=-4.80119 StartZ=0 EndX=-2.31591 EndY=-5.59111 EndZ=0
    g10: LineSegment StartX=-2.31591 StartY=-5.59111 StartZ=0 EndX=-0.789915 EndY=-6 EndZ=0
    g11: LineSegment StartX=-0.789915 StartY=-6 StartZ=0 EndX=0.789915 EndY=-6 EndZ=0
    g12: LineSegment StartX=0.789915 StartY=-6 StartZ=0 EndX=2.31591 EndY=-5.59111 EndZ=0
    g13: LineSegment StartX=2.31591 StartY=-5.59111 StartZ=0 EndX=3.68409 EndY=-4.80119 EndZ=0
    g14: LineSegment StartX=3.68409 StartY=-4.80119 StartZ=0 EndX=4.80119 EndY=-3.68409 EndZ=0
    g15: LineSegment StartX=4.80119 StartY=-3.68409 StartZ=0 EndX=5.59111 EndY=-2.31591 EndZ=0
    g16: LineSegment StartX=5.59111 StartY=-2.31591 StartZ=0 EndX=6 EndY=-0.789915 EndZ=0
    g17: LineSegment StartX=6 StartY=-0.789915 StartZ=0 EndX=6 EndY=0.789915 EndZ=0
    g18: LineSegment StartX=6 StartY=0.789915 StartZ=0 EndX=5.59111 EndY=2.31591 EndZ=0
    g19: LineSegment StartX=5.59111 StartY=2.31591 StartZ=0 EndX=4.80119 EndY=3.68409 EndZ=0
    g20: LineSegment StartX=4.80119 StartY=3.68409 StartZ=0 EndX=3.68409 EndY=4.80119 EndZ=0
    g21: LineSegment StartX=3.68409 StartY=4.80119 StartZ=0 EndX=2.31591 EndY=5.59111 EndZ=0
    g22: LineSegment StartX=2.31591 StartY=5.59111 StartZ=0 EndX=0.789915 EndY=6 EndZ=0
    g23: LineSegment StartX=0.789915 StartY=6 StartZ=0 EndX=-0.789915 EndY=6 EndZ=0
    g24: Circle [constr] CenterX=0 CenterY=0 CenterZ=0 NormalX=0 NormalY=0 NormalZ=1 AngleXU=0 Radius=6.05177
  constraints (52):
    c: Coincident(g0,g1)
    c: Coincident(g1,g2)
    c: Coincident(g2,g3)
    c: Coincident(g3,g4)
    c: Coincident(g4,g5)
    c: Coincident(g5,g6)
    c: Coincident(g6,g7)
    c: Coincident(g7,g8)
    c: Coincident(g8,g9)
    c: Coincident(g9,g10)
    c: Coincident(g10,g11)
    c: Coincident(g11,g12)
    c: Coincident(g12,g13)
    c: Coincident(g13,g14)
    c: Coincident(g14,g15)
    c: Coincident(g15,g16)
    c: Coincident(g16,g17)
    c: Coincident(g17,g18)
    c: Coincident(g18,g19)
    c: Coincident(g19,g20)
    c: Coincident(g20,g21)
    c: Coincident(g21,g22)
    c: Coincident(g22,g23)
    c: Coincident(g23,g0)
    c: Equal(g0, g1-g23) x23
    c: PointOnObject(g0,g24)
    c: PointOnObject(g1,g24)
    c: PointOnObject(g2,g24)
    c: PointOnObject(g3,g24)
    c: PointOnObject(g4,g24)
    c: PointOnObject(g5,g24)
    c: PointOnObject(g6,g24)
    c: PointOnObject(g7,g24)
    c: PointOnObject(g8,g24)
    c: PointOnObject(g9,g24)
    c: PointOnObject(g10,g24)
    c: PointOnObject(g11,g24)
    c: PointOnObject(g12,g24)
    c: PointOnObject(g13,g24)
    c: PointOnObject(g14,g24)
    c: PointOnObject(g15,g24)
    c: PointOnObject(g16,g24)
    c: PointOnObject(g17,g24)
    c: PointOnObject(g18,g24)
    c: PointOnObject(g19,g24)
    c: PointOnObject(g20,g24)
    c: PointOnObject(g21,g24)
    c: PointOnObject(g22,g24)
    c: PointOnObject(g23,g24)
    c: Coincident(g24,g-1)
    c: Horizontal(g23)
    c: DistanceX(g4,g17) = 12
FEATURE [Sketcher::SketchObject] Sketch019
  AttachmentOffset = pos=(0,0,7) rot=(0,0,1;0rad)
  MapMode = 5
  Placement = pos=(0,0,7) rot=(0,0,1;0rad)
  Support = -> [XY_Plane004]
  sketch-geometry (25):
    g0: LineSegment StartX=-0.724089 StartY=5.5 StartZ=0 EndX=-2.12292 EndY=5.12518 EndZ=0
    g1: LineSegment StartX=-2.12292 StartY=5.12518 StartZ=0 EndX=-3.37708 EndY=4.4011 EndZ=0
    g2: LineSegment StartX=-3.37708 StartY=4.4011 StartZ=0 EndX=-4.4011 EndY=3.37708 EndZ=0
    g3: LineSegment StartX=-4.4011 StartY=3.37708 StartZ=0 EndX=-5.12518 EndY=2.12292 EndZ=0
    g4: LineSegment StartX=-5.12518 StartY=2.12292 StartZ=0 EndX=-5.5 EndY=0.724089 EndZ=0
    g5: LineSegment StartX=-5.5 StartY=0.724089 StartZ=0 EndX=-5.5 EndY=-0.724089 EndZ=0
    g6: LineSegment StartX=-5.5 StartY=-0.724089 StartZ=0 EndX=-5.12518 EndY=-2.12292 EndZ=0
    g7: LineSegment StartX=-5.12518 StartY=-2.12292 StartZ=0 EndX=-4.4011 EndY=-3.37708 EndZ=0
    g8: LineSegment StartX=-4.4011 StartY=-3.37708 StartZ=0 EndX=-3.37708 EndY=-4.4011 EndZ=0
    g9: LineSegment StartX=-3.37708 StartY=-4.4011 StartZ=0 EndX=-2.12292 EndY=-5.12518 EndZ=0
    g10: LineSegment StartX=-2.12292 StartY=-5.12518 StartZ=0 EndX=-0.724089 EndY=-5.5 EndZ=0
    g11: LineSegment StartX=-0.724089 StartY=-5.5 StartZ=0 EndX=0.724089 EndY=-5.5 EndZ=0
    g12: LineSegment StartX=0.724089 StartY=-5.5 StartZ=0 EndX=2.12292 EndY=-5.12518 EndZ=0
    g13: LineSegment StartX=2.12292 StartY=-5.12518 StartZ=0 EndX=3.37708 EndY=-4.4011 EndZ=0
    g14: LineSegment StartX=3.37708 StartY=-4.4011 StartZ=0 EndX=4.4011 EndY=-3.37708 EndZ=0
    g15: LineSegment StartX=4.4011 StartY=-3.37708 StartZ=0 EndX=5.12518 EndY=-2.12292 EndZ=0
    g16: LineSegment StartX=5.12518 StartY=-2.12292 StartZ=0 EndX=5.5 EndY=-0.724089 EndZ=0
    g17: LineSegment StartX=5.5 StartY=-0.724089 StartZ=0 EndX=5.5 EndY=0.724089 EndZ=0
    g18: LineSegment StartX=5.5 StartY=0.724089 StartZ=0 EndX=5.12518 EndY=2.12292 EndZ=0
    g19: LineSegment StartX=5.12518 StartY=2.12292 StartZ=0 EndX=4.4011 EndY=3.37708 EndZ=0
    g20: LineSegment StartX=4.4011 StartY=3.37708 StartZ=0 EndX=3.37708 EndY=4.4011 EndZ=0
    g21: LineSegment StartX=3.37708 StartY=4.4011 StartZ=0 EndX=2.12292 EndY=5.12518 EndZ=0
    g22: LineSegment StartX=2.12292 StartY=5.12518 StartZ=0 EndX=0.724089 EndY=5.5 EndZ=0
    g23: LineSegment StartX=0.724089 StartY=5.5 StartZ=0 EndX=-0.724089 EndY=5.5 EndZ=0
    g24: Circle [constr] CenterX=0 CenterY=0 CenterZ=0 NormalX=0 NormalY=0 NormalZ=1 AngleXU=0 Radius=5.54746
  constraints (52):
    c: Coincident(g0,g1)
    c: Coincident(g1,g2)
    c: Coincident(g2,g3)
    c: Coincident(g3,g4)
    c: Coincident(g4,g5)
    c: Coincident(g5,g6)
    c: Coincident(g6,g7)
    c: Coincident(g7,g8)
    c: Coincident(g8,g9)
    c: Coincident(g9,g10)
    c: Coincident(g10,g11)
    c: Coincident(g11,g12)
    c: Coincident(g12,g13)
    c: Coincident(g13,g14)
    c: Coincident(g14,g15)
    c: Coincident(g15,g16)
    c: Coincident(g16,g17)
    c: Coincident(g17,g18)
    c: Coincident(g18,g19)
    c: Coincident(g19,g20)
    c: Coincident(g20,g21)
    c: Coincident(g21,g22)
    c: Coincident(g22,g23)
    c: Coincident(g23,g0)
    c: Equal(g0, g1-g23) x23
    c: PointOnObject(g0,g24)
    c: PointOnObject(g1,g24)
    c: PointOnObject(g2,g24)
    c: PointOnObject(g3,g24)
    c: PointOnObject(g4,g24)
    c: PointOnObject(g5,g24)
    c: PointOnObject(g6,g24)
    c: PointOnObject(g7,g24)
    c: PointOnObject(g8,g24)
    c: PointOnObject(g9,g24)
    c: PointOnObject(g10,g24)
    c: PointOnObject(g11,g24)
    c: PointOnObject(g12,g24)
    c: PointOnObject(g13,g24)
    c: PointOnObject(g14,g24)
    c: PointOnObject(g15,g24)
    c: PointOnObject(g16,g24)
    c: PointOnObject(g17,g24)
    c: PointOnObject(g18,g24)
    c: PointOnObject(g19,g24)
    c: PointOnObject(g20,g24)
    c: PointOnObject(g21,g24)
    c: PointOnObject(g22,g24)
    c: PointOnObject(g23,g24)
    c: Coincident(g24,g-1)
    c: Horizontal(g23)
    c: DistanceX(g4,g17) = 11
FEATURE [PartDesign::AdditiveLoft] AdditiveLoft002
  AllowMultiFace = false
  Closed = false
  Profile = -> Sketch018
  Refine = true
  Ruled = false
  Sections = -> [Sketch019,Sketch016]
FEATURE [Sketcher::SketchObject] Sketch017
  MapMode = 5
  Placement = pos=(0,0,17) rot=(0,0,1;0rad)
  Support = -> [AdditiveLoft002]
  sketch-geometry (1):
    g0: Circle CenterX=0 CenterY=0 CenterZ=0 NormalX=0 NormalY=0 NormalZ=1 AngleXU=0 Radius=4.5
  constraints (2):
    c: Coincident(g0,g-1)
    c: Radius(g0) = 4.5
FEATURE [PartDesign::Pad] Pad004
  AllowMultiFace = false
  BaseFeature = -> AdditiveLoft002
  Direction = (1,1,1)
  Length = 0.7
  Length2 = 100
  Profile = -> Sketch017
  Refine = true
  Type = 0
FEATURE [Sketcher::SketchObject] Sketch020
  MapMode = 5
  Placement = pos=(0,0,0) rot=(1,0,0;3.14159rad)
  Support = -> [Pad004]
  sketch-geometry (1):
    g0: Circle CenterX=0 CenterY=0 CenterZ=0 NormalX=0 NormalY=0 NormalZ=1 AngleXU=0 Radius=5
  constraints (2):
    c: Coincident(g0,g-1)
    c: Radius(g0) = 5
FEATURE [Sketcher::SketchObject] Sketch021
  MapMode = 5
  Placement = pos=(0,0,1) rot=(1,0,0;3.14159rad)
  sketch-geometry (1):
    g0: Circle CenterX=0 CenterY=0 CenterZ=0 NormalX=0 NormalY=0 NormalZ=1 AngleXU=0 Radius=4.65
  constraints (2):
    c: Coincident(g0,g-1)
    c: Radius(g0) = 4.65
FEATURE [Sketcher::SketchObject] Sketch022
  MapMode = 5
  Placement = pos=(0,0,2) rot=(1,0,0;3.14159rad)
  sketch-geometry (2):
    g0: ArcOfCircle CenterX=0 CenterY=0 CenterZ=0 NormalX=0 NormalY=0 NormalZ=1 AngleXU=0 Radius=3 StartAngle=2.19024 EndAngle=7.23453
    g1: LineSegment StartX=-1.74176 StartY=2.4426 StartZ=0 EndX=1.74176 EndY=2.4426 EndZ=0
  constraints (5):
    c: Coincident(g0,g-1)
    c: Coincident(g1,g0)
    c: Coincident(g1,g0)
    c: Horizontal(g1)
    c: Radius(g0) = 3
FEATURE [PartDesign::Body] Body004  label="Outer001"
  Group = -> [Sketch018,Sketch019,Sketch016,AdditiveLoft002,Sketch017,Pad004,Sketch020,Sketch021,Sketch022]
  Origin = -> Origin004
  Placement = pos=(10,-10,0) rot=(0,0,1;0rad)
  Tip = -> Pad004
FEATURE [Sketcher::SketchObject] Sketch023
  AttachmentOffset = pos=(0,0,17) rot=(0,0,1;0rad)
  MapMode = 5
  Placement = pos=(0,0,17) rot=(0,0,1;0rad)
  Support = -> [XY_Plane005]
  sketch-geometry (25):
    g0: LineSegment StartX=-4.65926 StartY=1.92993 StartZ=0 EndX=-5 EndY=0.658262 EndZ=0
    g1: LineSegment StartX=-5 StartY=0.658262 StartZ=0 EndX=-5 EndY=-0.658262 EndZ=0
    g2: LineSegment StartX=-5 StartY=-0.658262 StartZ=0 EndX=-4.65926 EndY=-1.92993 EndZ=0
    g3: LineSegment StartX=-4.65926 StartY=-1.92993 StartZ=0 EndX=-4.001 EndY=-3.07007 EndZ=0
    g4: LineSegment StartX=-4.001 StartY=-3.07007 StartZ=0 EndX=-3.07007 EndY=-4.001 EndZ=0
    g5: LineSegment StartX=-3.07007 StartY=-4.001 StartZ=0 EndX=-1.92993 EndY=-4.65926 EndZ=0
    g6: LineSegment StartX=-1.92993 StartY=-4.65926 StartZ=0 EndX=-0.658262 EndY=-5 EndZ=0
    g7: LineSegment StartX=-0.658262 StartY=-5 StartZ=0 EndX=0.658262 EndY=-5 EndZ=0
    g8: LineSegment StartX=0.658262 StartY=-5 StartZ=0 EndX=1.92993 EndY=-4.65926 EndZ=0
    g9: LineSegment StartX=1.92993 StartY=-4.65926 StartZ=0 EndX=3.07007 EndY=-4.001 EndZ=0
    g10: LineSegment StartX=3.07007 StartY=-4.001 StartZ=0 EndX=4.001 EndY=-3.07007 EndZ=0
    g11: LineSegment StartX=4.001 StartY=-3.07007 StartZ=0 EndX=4.65926 EndY=-1.92993 EndZ=0
    g12: LineSegment StartX=4.65926 StartY=-1.92993 StartZ=0 EndX=5 EndY=-0.658262 EndZ=0
    g13: LineSegment StartX=5 StartY=-0.658262 StartZ=0 EndX=5 EndY=0.658262 EndZ=0
    g14: LineSegment StartX=5 StartY=0.658262 StartZ=0 EndX=4.65926 EndY=1.92993 EndZ=0
    g15: LineSegment StartX=4.65926 StartY=1.92993 StartZ=0 EndX=4.001 EndY=3.07007 EndZ=0
    g16: LineSegment StartX=4.001 StartY=3.07007 StartZ=0 EndX=3.07007 EndY=4.001 EndZ=0
    g17: LineSegment StartX=3.07007 StartY=4.001 StartZ=0 EndX=1.92993 EndY=4.65926 EndZ=0
    g18: LineSegment StartX=1.92993 StartY=4.65926 StartZ=0 EndX=0.658262 EndY=5 EndZ=0
    g19: LineSegment StartX=0.658262 StartY=5 StartZ=0 EndX=-0.658262 EndY=5 EndZ=0
    g20: LineSegment StartX=-0.658262 StartY=5 StartZ=0 EndX=-1.92993 EndY=4.65926 EndZ=0
    g21: LineSegment StartX=-1.92993 StartY=4.65926 StartZ=0 EndX=-3.07007 EndY=4.001 EndZ=0
    g22: LineSegment StartX=-3.07007 StartY=4.001 StartZ=0 EndX=-4.001 EndY=3.07007 EndZ=0
    g23: LineSegment StartX=-4.001 StartY=3.07007 StartZ=0 EndX=-4.65926 EndY=1.92993 EndZ=0
    g24: Circle [constr] CenterX=0 CenterY=0 CenterZ=0 NormalX=0 NormalY=0 NormalZ=1 AngleXU=0 Radius=5.04314
  constraints (52):
    c: Coincident(g0,g1)
    c: Coincident(g1,g2)
    c: Coincident(g2,g3)
    c: Coincident(g3,g4)
    c: Coincident(g4,g5)
    c: Coincident(g5,g6)
    c: Coincident(g6,g7)
    c: Coincident(g7,g8)
    c: Coincident(g8,g9)
    c: Coincident(g9,g10)
    c: Coincident(g10,g11)
    c: Coincident(g11,g12)
    c: Coincident(g12,g13)
    c: Coincident(g13,g14)
    c: Coincident(g14,g15)
    c: Coincident(g15,g16)
    c: Coincident(g16,g17)
    c: Coincident(g17,g18)
    c: Coincident(g18,g19)
    c: Coincident(g19,g20)
    c: Coincident(g20,g21)
    c: Coincident(g21,g22)
    c: Coincident(g22,g23)
    c: Coincident(g23,g0)
    c: Equal(g0, g1-g23) x23
    c: PointOnObject(g0,g24)
    c: PointOnObject(g1,g24)
    c: PointOnObject(g2,g24)
    c: PointOnObject(g3,g24)
    c: PointOnObject(g4,g24)
    c: PointOnObject(g5,g24)
    c: PointOnObject(g6,g24)
    c: PointOnObject(g7,g24)
    c: PointOnObject(g8,g24)
    c: PointOnObject(g9,g24)
    c: PointOnObject(g10,g24)
    c: PointOnObject(g11,g24)
    c: PointOnObject(g12,g24)
    c: PointOnObject(g13,g24)
    c: PointOnObject(g14,g24)
    c: PointOnObject(g15,g24)
    c: PointOnObject(g16,g24)
    c: PointOnObject(g17,g24)
    c: PointOnObject(g18,g24)
    c: PointOnObject(g19,g24)
    c: PointOnObject(g20,g24)
    c: PointOnObject(g21,g24)
    c: PointOnObject(g22,g24)
    c: PointOnObject(g23,g24)
    c: Coincident(g24,g-1)
    c: Horizontal(g19)
    c: DistanceX(g0,g13) = 10
FEATURE [Sketcher::SketchObject] Sketch025
  MapMode = 5
  Support = -> [XY_Plane005]
  sketch-geometry (25):
    g0: LineSegment StartX=-0.789915 StartY=6 StartZ=0 EndX=-2.31591 EndY=5.59111 EndZ=0
    g1: LineSegment StartX=-2.31591 StartY=5.59111 StartZ=0 EndX=-3.68409 EndY=4.80119 EndZ=0
    g2: LineSegment StartX=-3.68409 StartY=4.80119 StartZ=0 EndX=-4.80119 EndY=3.68409 EndZ=0
    g3: LineSegment StartX=-4.80119 StartY=3.68409 StartZ=0 EndX=-5.59111 EndY=2.31591 EndZ=0
    g4: LineSegment StartX=-5.59111 StartY=2.31591 StartZ=0 EndX=-6 EndY=0.789915 EndZ=0
    g5: LineSegment StartX=-6 StartY=0.789915 StartZ=0 EndX=-6 EndY=-0.789915 EndZ=0
    g6: LineSegment StartX=-6 StartY=-0.789915 StartZ=0 EndX=-5.59111 EndY=-2.31591 EndZ=0
    g7: LineSegment StartX=-5.59111 StartY=-2.31591 StartZ=0 EndX=-4.80119 EndY=-3.68409 EndZ=0
    g8: LineSegment StartX=-4.80119 StartY=-3.68409 StartZ=0 EndX=-3.68409 EndY=-4.80119 EndZ=0
    g9: LineSegment StartX=-3.68409 StartY=-4.80119 StartZ=0 EndX=-2.31591 EndY=-5.59111 EndZ=0
    g10: LineSegment StartX=-2.31591 StartY=-5.59111 StartZ=0 EndX=-0.789915 EndY=-6 EndZ=0
    g11: LineSegment StartX=-0.789915 StartY=-6 StartZ=0 EndX=0.789915 EndY=-6 EndZ=0
    g12: LineSegment StartX=0.789915 StartY=-6 StartZ=0 EndX=2.31591 EndY=-5.59111 EndZ=0
    g13: LineSegment StartX=2.31591 StartY=-5.59111 StartZ=0 EndX=3.68409 EndY=-4.80119 EndZ=0
    g14: LineSegment StartX=3.68409 StartY=-4.80119 StartZ=0 EndX=4.80119 EndY=-3.68409 EndZ=0
    g15: LineSegment StartX=4.80119 StartY=-3.68409 StartZ=0 EndX=5.59111 EndY=-2.31591 EndZ=0
    g16: LineSegment StartX=5.59111 StartY=-2.31591 StartZ=0 EndX=6 EndY=-0.789915 EndZ=0
    g17: LineSegment StartX=6 StartY=-0.789915 StartZ=0 EndX=6 EndY=0.789915 EndZ=0
    g18: LineSegment StartX=6 StartY=0.789915 StartZ=0 EndX=5.59111 EndY=2.31591 EndZ=0
    g19: LineSegment StartX=5.59111 StartY=2.31591 StartZ=0 EndX=4.80119 EndY=3.68409 EndZ=0
    g20: LineSegment StartX=4.80119 StartY=3.68409 StartZ=0 EndX=3.68409 EndY=4.80119 EndZ=0
    g21: LineSegment StartX=3.68409 StartY=4.80119 StartZ=0 EndX=2.31591 EndY=5.59111 EndZ=0
    g22: LineSegment StartX=2.31591 StartY=5.59111 StartZ=0 EndX=0.789915 EndY=6 EndZ=0
    g23: LineSegment StartX=0.789915 StartY=6 StartZ=0 EndX=-0.789915 EndY=6 EndZ=0
    g24: Circle [constr] CenterX=0 CenterY=0 CenterZ=0 NormalX=0 NormalY=0 NormalZ=1 AngleXU=0 Radius=6.05177
  constraints (52):
    c: Coincident(g0,g1)
    c: Coincident(g1,g2)
    c: Coincident(g2,g3)
    c: Coincident(g3,g4)
    c: Coincident(g4,g5)
    c: Coincident(g5,g6)
    c: Coincident(g6,g7)
    c: Coincident(g7,g8)
    c: Coincident(g8,g9)
    c: Coincident(g9,g10)
    c: Coincident(g10,g11)
    c: Coincident(g11,g12)
    c: Coincident(g12,g13)
    c: Coincident(g13,g14)
    c: Coincident(g14,g15)
    c: Coincident(g15,g16)
    c: Coincident(g16,g17)
    c: Coincident(g17,g18)
    c: Coincident(g18,g19)
    c: Coincident(g19,g20)
    c: Coincident(g20,g21)
    c: Coincident(g21,g22)
    c: Coincident(g22,g23)
    c: Coincident(g23,g0)
    c: Equal(g0, g1-g23) x23
    c: PointOnObject(g0,g24)
    c: PointOnObject(g1,g24)
    c: PointOnObject(g2,g24)
    c: PointOnObject(g3,g24)
    c: PointOnObject(g4,g24)
    c: PointOnObject(g5,g24)
    c: PointOnObject(g6,g24)
    c: PointOnObject(g7,g24)
    c: PointOnObject(g8,g24)
    c: PointOnObject(g9,g24)
    c: PointOnObject(g10,g24)
    c: PointOnObject(g11,g24)
    c: PointOnObject(g12,g24)
    c: PointOnObject(g13,g24)
    c: PointOnObject(g14,g24)
    c: PointOnObject(g15,g24)
    c: PointOnObject(g16,g24)
    c: PointOnObject(g17,g24)
    c: PointOnObject(g18,g24)
    c: PointOnObject(g19,g24)
    c: PointOnObject(g20,g24)
    c: PointOnObject(g21,g24)
    c: PointOnObject(g22,g24)
    c: PointOnObject(g23,g24)
    c: Coincident(g24,g-1)
    c: Horizontal(g23)
    c: DistanceX(g4,g17) = 12
FEATURE [Sketcher::SketchObject] Sketch026
  AttachmentOffset = pos=(0,0,7) rot=(0,0,1;0rad)
  MapMode = 5
  Placement = pos=(0,0,7) rot=(0,0,1;0rad)
  Support = -> [XY_Plane005]
  sketch-geometry (25):
    g0: LineSegment StartX=-0.724089 StartY=5.5 StartZ=0 EndX=-2.12292 EndY=5.12518 EndZ=0
    g1: LineSegment StartX=-2.12292 StartY=5.12518 StartZ=0 EndX=-3.37708 EndY=4.4011 EndZ=0
    g2: LineSegment StartX=-3.37708 StartY=4.4011 StartZ=0 EndX=-4.4011 EndY=3.37708 EndZ=0
    g3: LineSegment StartX=-4.4011 StartY=3.37708 StartZ=0 EndX=-5.12518 EndY=2.12292 EndZ=0
    g4: LineSegment StartX=-5.12518 StartY=2.12292 StartZ=0 EndX=-5.5 EndY=0.724089 EndZ=0
    g5: LineSegment StartX=-5.5 StartY=0.724089 StartZ=0 EndX=-5.5 EndY=-0.724089 EndZ=0
    g6: LineSegment StartX=-5.5 StartY=-0.724089 StartZ=0 EndX=-5.12518 EndY=-2.12292 EndZ=0
    g7: LineSegment StartX=-5.12518 StartY=-2.12292 StartZ=0 EndX=-4.4011 EndY=-3.37708 EndZ=0
    g8: LineSegment StartX=-4.4011 StartY=-3.37708 StartZ=0 EndX=-3.37708 EndY=-4.4011 EndZ=0
    g9: LineSegment StartX=-3.37708 StartY=-4.4011 StartZ=0 EndX=-2.12292 EndY=-5.12518 EndZ=0
    g10: LineSegment StartX=-2.12292 StartY=-5.12518 StartZ=0 EndX=-0.724089 EndY=-5.5 EndZ=0
    g11: LineSegment StartX=-0.724089 StartY=-5.5 StartZ=0 EndX=0.724089 EndY=-5.5 EndZ=0
    g12: LineSegment StartX=0.724089 StartY=-5.5 StartZ=0 EndX=2.12292 EndY=-5.12518 EndZ=0
    g13: LineSegment StartX=2.12292 StartY=-5.12518 StartZ=0 EndX=3.37708 EndY=-4.4011 EndZ=0
    g14: LineSegment StartX=3.37708 StartY=-4.4011 StartZ=0 EndX=4.4011 EndY=-3.37708 EndZ=0
    g15: LineSegment StartX=4.4011 StartY=-3.37708 StartZ=0 EndX=5.12518 EndY=-2.12292 EndZ=0
    g16: LineSegment StartX=5.12518 StartY=-2.12292 StartZ=0 EndX=5.5 EndY=-0.724089 EndZ=0
    g17: LineSegment StartX=5.5 StartY=-0.724089 StartZ=0 EndX=5.5 EndY=0.724089 EndZ=0
    g18: LineSegment StartX=5.5 StartY=0.724089 StartZ=0 EndX=5.12518 EndY=2.12292 EndZ=0
    g19: LineSegment StartX=5.12518 StartY=2.12292 StartZ=0 EndX=4.4011 EndY=3.37708 EndZ=0
    g20: LineSegment StartX=4.4011 StartY=3.37708 StartZ=0 EndX=3.37708 EndY=4.4011 EndZ=0
    g21: LineSegment StartX=3.37708 StartY=4.4011 StartZ=0 EndX=2.12292 EndY=5.12518 EndZ=0
    g22: LineSegment StartX=2.12292 StartY=5.12518 StartZ=0 EndX=0.724089 EndY=5.5 EndZ=0
    g23: LineSegment StartX=0.724089 StartY=5.5 StartZ=0 EndX=-0.724089 EndY=5.5 EndZ=0
    g24: Circle [constr] CenterX=0 CenterY=0 CenterZ=0 NormalX=0 NormalY=0 NormalZ=1 AngleXU=0 Radius=5.54746
  constraints (52):
    c: Coincident(g0,g1)
    c: Coincident(g1,g2)
    c: Coincident(g2,g3)
    c: Coincident(g3,g4)
    c: Coincident(g4,g5)
    c: Coincident(g5,g6)
    c: Coincident(g6,g7)
    c: Coincident(g7,g8)
    c: Coincident(g8,g9)
    c: Coincident(g9,g10)
    c: Coincident(g10,g11)
    c: Coincident(g11,g12)
    c: Coincident(g12,g13)
    c: Coincident(g13,g14)
    c: Coincident(g14,g15)
    c: Coincident(g15,g16)
    c: Coincident(g16,g17)
    c: Coincident(g17,g18)
    c: Coincident(g18,g19)
    c: Coincident(g19,g20)
    c: Coincident(g20,g21)
    c: Coincident(g21,g22)
    c: Coincident(g22,g23)
    c: Coincident(g23,g0)
    c: Equal(g0, g1-g23) x23
    c: PointOnObject(g0,g24)
    c: PointOnObject(g1,g24)
    c: PointOnObject(g2,g24)
    c: PointOnObject(g3,g24)
    c: PointOnObject(g4,g24)
    c: PointOnObject(g5,g24)
    c: PointOnObject(g6,g24)
    c: PointOnObject(g7,g24)
    c: PointOnObject(g8,g24)
    c: PointOnObject(g9,g24)
    c: PointOnObject(g10,g24)
    c: PointOnObject(g11,g24)
    c: PointOnObject(g12,g24)
    c: PointOnObject(g13,g24)
    c: PointOnObject(g14,g24)
    c: PointOnObject(g15,g24)
    c: PointOnObject(g16,g24)
    c: PointOnObject(g17,g24)
    c: PointOnObject(g18,g24)
    c: PointOnObject(g19,g24)
    c: PointOnObject(g20,g24)
    c: PointOnObject(g21,g24)
    c: PointOnObject(g22,g24)
    c: PointOnObject(g23,g24)
    c: Coincident(g24,g-1)
    c: Horizontal(g23)
    c: DistanceX(g4,g17) = 11
FEATURE [PartDesign::AdditiveLoft] AdditiveLoft003
  AllowMultiFace = false
  Closed = false
  Profile = -> Sketch025
  Refine = true
  Ruled = false
  Sections = -> [Sketch026,Sketch023]
FEATURE [Sketcher::SketchObject] Sketch024
  MapMode = 5
  Placement = pos=(0,0,17) rot=(0,0,1;0rad)
  Support = -> [AdditiveLoft003]
  sketch-geometry (1):
    g0: Circle CenterX=0 CenterY=0 CenterZ=0 NormalX=0 NormalY=0 NormalZ=1 AngleXU=0 Radius=4.5
  constraints (2):
    c: Coincident(g0,g-1)
    c: Radius(g0) = 4.5
FEATURE [PartDesign::Pad] Pad005
  AllowMultiFace = false
  BaseFeature = -> AdditiveLoft003
  Direction = (1,1,1)
  Length = 0.7
  Length2 = 100
  Profile = -> Sketch024
  Refine = true
  Type = 0
FEATURE [Sketcher::SketchObject] Sketch027
  MapMode = 5
  Placement = pos=(0,0,0) rot=(1,0,0;3.14159rad)
  Support = -> [Pad005]
  sketch-geometry (1):
    g0: Circle CenterX=0 CenterY=0 CenterZ=0 NormalX=0 NormalY=0 NormalZ=1 AngleXU=0 Radius=5
  constraints (2):
    c: Coincident(g0,g-1)
    c: Radius(g0) = 5
FEATURE [Sketcher::SketchObject] Sketch028
  MapMode = 5
  Placement = pos=(0,0,1) rot=(1,0,0;3.14159rad)
  sketch-geometry (1):
    g0: Circle CenterX=0 CenterY=0 CenterZ=0 NormalX=0 NormalY=0 NormalZ=1 AngleXU=0 Radius=4.65
  constraints (2):
    c: Coincident(g0,g-1)
    c: Radius(g0) = 4.65
FEATURE [Sketcher::SketchObject] Sketch029
  MapMode = 5
  Placement = pos=(0,0,2) rot=(1,0,0;3.14159rad)
  sketch-geometry (2):
    g0: ArcOfCircle CenterX=0 CenterY=0 CenterZ=0 NormalX=0 NormalY=0 NormalZ=1 AngleXU=0 Radius=3 StartAngle=2.19024 EndAngle=7.23453
    g1: LineSegment StartX=-1.74176 StartY=2.4426 StartZ=0 EndX=1.74176 EndY=2.4426 EndZ=0
  constraints (5):
    c: Coincident(g0,g-1)
    c: Coincident(g1,g0)
    c: Coincident(g1,g0)
    c: Horizontal(g1)
    c: Radius(g0) = 3
FEATURE [PartDesign::Body] Body005  label="Outer002"
  Group = -> [Sketch025,Sketch026,Sketch023,AdditiveLoft003,Sketch024,Pad005,Sketch027,Sketch028,Sketch029]
  Origin = -> Origin005
  Placement = pos=(10,10,0) rot=(0,0,1;0rad)
  Tip = -> Pad005
FEATURE [Sketcher::SketchObject] Sketch030
  AttachmentOffset = pos=(0,0,17) rot=(0,0,1;0rad)
  MapMode = 5
  Placement = pos=(0,0,17) rot=(0,0,1;0rad)
  Support = -> [XY_Plane006]
  sketch-geometry (25):
    g0: LineSegment StartX=-4.65926 StartY=1.92993 StartZ=0 EndX=-5 EndY=0.658262 EndZ=0
    g1: LineSegment StartX=-5 StartY=0.658262 StartZ=0 EndX=-5 EndY=-0.658262 EndZ=0
    g2: LineSegment StartX=-5 StartY=-0.658262 StartZ=0 EndX=-4.65926 EndY=-1.92993 EndZ=0
    g3: LineSegment StartX=-4.65926 StartY=-1.92993 StartZ=0 EndX=-4.001 EndY=-3.07007 EndZ=0
    g4: LineSegment StartX=-4.001 StartY=-3.07007 StartZ=0 EndX=-3.07007 EndY=-4.001 EndZ=0
    g5: LineSegment StartX=-3.07007 StartY=-4.001 StartZ=0 EndX=-1.92993 EndY=-4.65926 EndZ=0
    g6: LineSegment StartX=-1.92993 StartY=-4.65926 StartZ=0 EndX=-0.658262 EndY=-5 EndZ=0
    g7: LineSegment StartX=-0.658262 StartY=-5 StartZ=0 EndX=0.658262 EndY=-5 EndZ=0
    g8: LineSegment StartX=0.658262 StartY=-5 StartZ=0 EndX=1.92993 EndY=-4.65926 EndZ=0
    g9: LineSegment StartX=1.92993 StartY=-4.65926 StartZ=0 EndX=3.07007 EndY=-4.001 EndZ=0
    g10: LineSegment StartX=3.07007 StartY=-4.001 StartZ=0 EndX=4.001 EndY=-3.07007 EndZ=0
    g11: LineSegment StartX=4.001 StartY=-3.07007 StartZ=0 EndX=4.65926 EndY=-1.92993 EndZ=0
    g12: LineSegment StartX=4.65926 StartY=-1.92993 StartZ=0 EndX=5 EndY=-0.658262 EndZ=0
    g13: LineSegment StartX=5 StartY=-0.658262 StartZ=0 EndX=5 EndY=0.658262 EndZ=0
    g14: LineSegment StartX=5 StartY=0.658262 StartZ=0 EndX=4.65926 EndY=1.92993 EndZ=0
    g15: LineSegment StartX=4.65926 StartY=1.92993 StartZ=0 EndX=4.001 EndY=3.07007 EndZ=0
    g16: LineSegment StartX=4.001 StartY=3.07007 StartZ=0 EndX=3.07007 EndY=4.001 EndZ=0
    g17: LineSegment StartX=3.07007 StartY=4.001 StartZ=0 EndX=1.92993 EndY=4.65926 EndZ=0
    g18: LineSegment StartX=1.92993 StartY=4.65926 StartZ=0 EndX=0.658262 EndY=5 EndZ=0
    g19: LineSegment StartX=0.658262 StartY=5 StartZ=0 EndX=-0.658262 EndY=5 EndZ=0
    g20: LineSegment StartX=-0.658262 StartY=5 StartZ=0 EndX=-1.92993 EndY=4.65926 EndZ=0
    g21: LineSegment StartX=-1.92993 StartY=4.65926 StartZ=0 EndX=-3.07007 EndY=4.001 EndZ=0
    g22: LineSegment StartX=-3.07007 StartY=4.001 StartZ=0 EndX=-4.001 EndY=3.07007 EndZ=0
    g23: LineSegment StartX=-4.001 StartY=3.07007 StartZ=0 EndX=-4.65926 EndY=1.92993 EndZ=0
    g24: Circle [constr] CenterX=0 CenterY=0 CenterZ=0 NormalX=0 NormalY=0 NormalZ=1 AngleXU=0 Radius=5.04314
  constraints (52):
    c: Coincident(g0,g1)
    c: Coincident(g1,g2)
    c: Coincident(g2,g3)
    c: Coincident(g3,g4)
    c: Coincident(g4,g5)
    c: Coincident(g5,g6)
    c: Coincident(g6,g7)
    c: Coincident(g7,g8)
    c: Coincident(g8,g9)
    c: Coincident(g9,g10)
    c: Coincident(g10,g11)
    c: Coincident(g11,g12)
    c: Coincident(g12,g13)
    c: Coincident(g13,g14)
    c: Coincident(g14,g15)
    c: Coincident(g15,g16)
    c: Coincident(g16,g17)
    c: Coincident(g17,g18)
    c: Coincident(g18,g19)
    c: Coincident(g19,g20)
    c: Coincident(g20,g21)
    c: Coincident(g21,g22)
    c: Coincident(g22,g23)
    c: Coincident(g23,g0)
    c: Equal(g0, g1-g23) x23
    c: PointOnObject(g0,g24)
    c: PointOnObject(g1,g24)
    c: PointOnObject(g2,g24)
    c: PointOnObject(g3,g24)
    c: PointOnObject(g4,g24)
    c: PointOnObject(g5,g24)
    c: PointOnObject(g6,g24)
    c: PointOnObject(g7,g24)
    c: PointOnObject(g8,g24)
    c: PointOnObject(g9,g24)
    c: PointOnObject(g10,g24)
    c: PointOnObject(g11,g24)
    c: PointOnObject(g12,g24)
    c: PointOnObject(g13,g24)
    c: PointOnObject(g14,g24)
    c: PointOnObject(g15,g24)
    c: PointOnObject(g16,g24)
    c: PointOnObject(g17,g24)
    c: PointOnObject(g18,g24)
    c: PointOnObject(g19,g24)
    c: PointOnObject(g20,g24)
    c: PointOnObject(g21,g24)
    c: PointOnObject(g22,g24)
    c: PointOnObject(g23,g24)
    c: Coincident(g24,g-1)
    c: Horizontal(g19)
    c: DistanceX(g0,g13) = 10
FEATURE [Sketcher::SketchObject] Sketch032
  MapMode = 5
  Support = -> [XY_Plane006]
  sketch-geometry (25):
    g0: LineSegment StartX=-0.789915 StartY=6 StartZ=0 EndX=-2.31591 EndY=5.59111 EndZ=0
    g1: LineSegment StartX=-2.31591 StartY=5.59111 StartZ=0 EndX=-3.68409 EndY=4.80119 EndZ=0
    g2: LineSegment StartX=-3.68409 StartY=4.80119 StartZ=0 EndX=-4.80119 EndY=3.68409 EndZ=0
    g3: LineSegment StartX=-4.80119 StartY=3.68409 StartZ=0 EndX=-5.59111 EndY=2.31591 EndZ=0
    g4: LineSegment StartX=-5.59111 StartY=2.31591 StartZ=0 EndX=-6 EndY=0.789915 EndZ=0
    g5: LineSegment StartX=-6 StartY=0.789915 StartZ=0 EndX=-6 EndY=-0.789915 EndZ=0
    g6: LineSegment StartX=-6 StartY=-0.789915 StartZ=0 EndX=-5.59111 EndY=-2.31591 EndZ=0
    g7: LineSegment StartX=-5.59111 StartY=-2.31591 StartZ=0 EndX=-4.80119 EndY=-3.68409 EndZ=0
    g8: LineSegment StartX=-4.80119 StartY=-3.68409 StartZ=0 EndX=-3.68409 EndY=-4.80119 EndZ=0
    g9: LineSegment StartX=-3.68409 StartY=-4.80119 StartZ=0 EndX=-2.31591 EndY=-5.59111 EndZ=0
    g10: LineSegment StartX=-2.31591 StartY=-5.59111 StartZ=0 EndX=-0.789915 EndY=-6 EndZ=0
    g11: LineSegment StartX=-0.789915 StartY=-6 StartZ=0 EndX=0.789915 EndY=-6 EndZ=0
    g12: LineSegment StartX=0.789915 StartY=-6 StartZ=0 EndX=2.31591 EndY=-5.59111 EndZ=0
    g13: LineSegment StartX=2.31591 StartY=-5.59111 StartZ=0 EndX=3.68409 EndY=-4.80119 EndZ=0
    g14: LineSegment StartX=3.68409 StartY=-4.80119 StartZ=0 EndX=4.80119 EndY=-3.68409 EndZ=0
    g15: LineSegment StartX=4.80119 StartY=-3.68409 StartZ=0 EndX=5.59111 EndY=-2.31591 EndZ=0
    g16: LineSegment StartX=5.59111 StartY=-2.31591 StartZ=0 EndX=6 EndY=-0.789915 EndZ=0
    g17: LineSegment StartX=6 StartY=-0.789915 StartZ=0 EndX=6 EndY=0.789915 EndZ=0
    g18: LineSegment StartX=6 StartY=0.789915 StartZ=0 EndX=5.59111 EndY=2.31591 EndZ=0
    g19: LineSegment StartX=5.59111 StartY=2.31591 StartZ=0 EndX=4.80119 EndY=3.68409 EndZ=0
    g20: LineSegment StartX=4.80119 StartY=3.68409 StartZ=0 EndX=3.68409 EndY=4.80119 EndZ=0
    g21: LineSegment StartX=3.68409 StartY=4.80119 StartZ=0 EndX=2.31591 EndY=5.59111 EndZ=0
    g22: LineSegment StartX=2.31591 StartY=5.59111 StartZ=0 EndX=0.789915 EndY=6 EndZ=0
    g23: LineSegment StartX=0.789915 StartY=6 StartZ=0 EndX=-0.789915 EndY=6 EndZ=0
    g24: Circle [constr] CenterX=0 CenterY=0 CenterZ=0 NormalX=0 NormalY=0 NormalZ=1 AngleXU=0 Radius=6.05177
  constraints (52):
    c: Coincident(g0,g1)
    c: Coincident(g1,g2)
    c: Coincident(g2,g3)
    c: Coincident(g3,g4)
    c: Coincident(g4,g5)
    c: Coincident(g5,g6)
    c: Coincident(g6,g7)
    c: Coincident(g7,g8)
    c: Coincident(g8,g9)
    c: Coincident(g9,g10)
    c: Coincident(g10,g11)
    c: Coincident(g11,g12)
    c: Coincident(g12,g13)
    c: Coincident(g13,g14)
    c: Coincident(g14,g15)
    c: Coincident(g15,g16)
    c: Coincident(g16,g17)
    c: Coincident(g17,g18)
    c: Coincident(g18,g19)
    c: Coincident(g19,g20)
    c: Coincident(g20,g21)
    c: Coincident(g21,g22)
    c: Coincident(g22,g23)
    c: Coincident(g23,g0)
    c: Equal(g0, g1-g23) x23
    c: PointOnObject(g0,g24)
    c: PointOnObject(g1,g24)
    c: PointOnObject(g2,g24)
    c: PointOnObject(g3,g24)
    c: PointOnObject(g4,g24)
    c: PointOnObject(g5,g24)
    c: PointOnObject(g6,g24)
    c: PointOnObject(g7,g24)
    c: PointOnObject(g8,g24)
    c: PointOnObject(g9,g24)
    c: PointOnObject(g10,g24)
    c: PointOnObject(g11,g24)
    c: PointOnObject(g12,g24)
    c: PointOnObject(g13,g24)
    c: PointOnObject(g14,g24)
    c: PointOnObject(g15,g24)
    c: PointOnObject(g16,g24)
    c: PointOnObject(g17,g24)
    c: PointOnObject(g18,g24)
    c: PointOnObject(g19,g24)
    c: PointOnObject(g20,g24)
    c: PointOnObject(g21,g24)
    c: PointOnObject(g22,g24)
    c: PointOnObject(g23,g24)
    c: Coincident(g24,g-1)
    c: Horizontal(g23)
    c: DistanceX(g4,g17) = 12
FEATURE [Sketcher::SketchObject] Sketch033
  AttachmentOffset = pos=(0,0,7) rot=(0,0,1;0rad)
  MapMode = 5
  Placement = pos=(0,0,7) rot=(0,0,1;0rad)
  Support = -> [XY_Plane006]
  sketch-geometry (25):
    g0: LineSegment StartX=-0.724089 StartY=5.5 StartZ=0 EndX=-2.12292 EndY=5.12518 EndZ=0
    g1: LineSegment StartX=-2.12292 StartY=5.12518 StartZ=0 EndX=-3.37708 EndY=4.4011 EndZ=0
    g2: LineSegment StartX=-3.37708 StartY=4.4011 StartZ=0 EndX=-4.4011 EndY=3.37708 EndZ=0
    g3: LineSegment StartX=-4.4011 StartY=3.37708 StartZ=0 EndX=-5.12518 EndY=2.12292 EndZ=0
    g4: LineSegment StartX=-5.12518 StartY=2.12292 StartZ=0 EndX=-5.5 EndY=0.724089 EndZ=0
    g5: LineSegment StartX=-5.5 StartY=0.724089 StartZ=0 EndX=-5.5 EndY=-0.724089 EndZ=0
    g6: LineSegment StartX=-5.5 StartY=-0.724089 StartZ=0 EndX=-5.12518 EndY=-2.12292 EndZ=0
    g7: LineSegment StartX=-5.12518 StartY=-2.12292 StartZ=0 EndX=-4.4011 EndY=-3.37708 EndZ=0
    g8: LineSegment StartX=-4.4011 StartY=-3.37708 StartZ=0 EndX=-3.37708 EndY=-4.4011 EndZ=0
    g9: LineSegment StartX=-3.37708 StartY=-4.4011 StartZ=0 EndX=-2.12292 EndY=-5.12518 EndZ=0
    g10: LineSegment StartX=-2.12292 StartY=-5.12518 StartZ=0 EndX=-0.724089 EndY=-5.5 EndZ=0
    g11: LineSegment StartX=-0.724089 StartY=-5.5 StartZ=0 EndX=0.724089 EndY=-5.5 EndZ=0
    g12: LineSegment StartX=0.724089 StartY=-5.5 StartZ=0 EndX=2.12292 EndY=-5.12518 EndZ=0
    g13: LineSegment StartX=2.12292 StartY=-5.12518 StartZ=0 EndX=3.37708 EndY=-4.4011 EndZ=0
    g14: LineSegment StartX=3.37708 StartY=-4.4011 StartZ=0 EndX=4.4011 EndY=-3.37708 EndZ=0
    g15: LineSegment StartX=4.4011 StartY=-3.37708 StartZ=0 EndX=5.12518 EndY=-2.12292 EndZ=0
    g16: LineSegment StartX=5.12518 StartY=-2.12292 StartZ=0 EndX=5.5 EndY=-0.724089 EndZ=0
    g17: LineSegment StartX=5.5 StartY=-0.724089 StartZ=0 EndX=5.5 EndY=0.724089 EndZ=0
    g18: LineSegment StartX=5.5 StartY=0.724089 StartZ=0 EndX=5.12518 EndY=2.12292 EndZ=0
    g19: LineSegment StartX=5.12518 StartY=2.12292 StartZ=0 EndX=4.4011 EndY=3.37708 EndZ=0
    g20: LineSegment StartX=4.4011 StartY=3.37708 StartZ=0 EndX=3.37708 EndY=4.4011 EndZ=0
    g21: LineSegment StartX=3.37708 StartY=4.4011 StartZ=0 EndX=2.12292 EndY=5.12518 EndZ=0
    g22: LineSegment StartX=2.12292 StartY=5.12518 StartZ=0 EndX=0.724089 EndY=5.5 EndZ=0
    g23: LineSegment StartX=0.724089 StartY=5.5 StartZ=0 EndX=-0.724089 EndY=5.5 EndZ=0
    g24: Circle [constr] CenterX=0 CenterY=0 CenterZ=0 NormalX=0 NormalY=0 NormalZ=1 AngleXU=0 Radius=5.54746
  constraints (52):
    c: Coincident(g0,g1)
    c: Coincident(g1,g2)
    c: Coincident(g2,g3)
    c: Coincident(g3,g4)
    c: Coincident(g4,g5)
    c: Coincident(g5,g6)
    c: Coincident(g6,g7)
    c: Coincident(g7,g8)
    c: Coincident(g8,g9)
    c: Coincident(g9,g10)
    c: Coincident(g10,g11)
    c: Coincident(g11,g12)
    c: Coincident(g12,g13)
    c: Coincident(g13,g14)
    c: Coincident(g14,g15)
    c: Coincident(g15,g16)
    c: Coincident(g16,g17)
    c: Coincident(g17,g18)
    c: Coincident(g18,g19)
    c: Coincident(g19,g20)
    c: Coincident(g20,g21)
    c: Coincident(g21,g22)
    c: Coincident(g22,g23)
    c: Coincident(g23,g0)
    c: Equal(g0, g1-g23) x23
    c: PointOnObject(g0,g24)
    c: PointOnObject(g1,g24)
    c: PointOnObject(g2,g24)
    c: PointOnObject(g3,g24)
    c: PointOnObject(g4,g24)
    c: PointOnObject(g5,g24)
    c: PointOnObject(g6,g24)
    c: PointOnObject(g7,g24)
    c: PointOnObject(g8,g24)
    c: PointOnObject(g9,g24)
    c: PointOnObject(g10,g24)
    c: PointOnObject(g11,g24)
    c: PointOnObject(g12,g24)
    c: PointOnObject(g13,g24)
    c: PointOnObject(g14,g24)
    c: PointOnObject(g15,g24)
    c: PointOnObject(g16,g24)
    c: PointOnObject(g17,g24)
    c: PointOnObject(g18,g24)
    c: PointOnObject(g19,g24)
    c: PointOnObject(g20,g24)
    c: PointOnObject(g21,g24)
    c: PointOnObject(g22,g24)
    c: PointOnObject(g23,g24)
    c: Coincident(g24,g-1)
    c: Horizontal(g23)
    c: DistanceX(g4,g17) = 11
FEATURE [PartDesign::AdditiveLoft] AdditiveLoft004
  AllowMultiFace = false
  Closed = false
  Profile = -> Sketch032
  Refine = true
  Ruled = false
  Sections = -> [Sketch033,Sketch030]
FEATURE [Sketcher::SketchObject] Sketch031
  MapMode = 5
  Placement = pos=(0,0,17) rot=(0,0,1;0rad)
  Support = -> [AdditiveLoft004]
  sketch-geometry (1):
    g0: Circle CenterX=0 CenterY=0 CenterZ=0 NormalX=0 NormalY=0 NormalZ=1 AngleXU=0 Radius=4.5
  constraints (2):
    c: Coincident(g0,g-1)
    c: Radius(g0) = 4.5
FEATURE [PartDesign::Pad] Pad006
  AllowMultiFace = false
  BaseFeature = -> AdditiveLoft004
  Direction = (1,1,1)
  Length = 0.7
  Length2 = 100
  Profile = -> Sketch031
  Refine = true
  Type = 0
FEATURE [Sketcher::SketchObject] Sketch034
  MapMode = 5
  Placement = pos=(0,0,0) rot=(1,0,0;3.14159rad)
  Support = -> [Pad006]
  sketch-geometry (1):
    g0: Circle CenterX=0 CenterY=0 CenterZ=0 NormalX=0 NormalY=0 NormalZ=1 AngleXU=0 Radius=5
  constraints (2):
    c: Coincident(g0,g-1)
    c: Radius(g0) = 5
FEATURE [Sketcher::SketchObject] Sketch035
  MapMode = 5
  Placement = pos=(0,0,1) rot=(1,0,0;3.14159rad)
  sketch-geometry (1):
    g0: Circle CenterX=0 CenterY=0 CenterZ=0 NormalX=0 NormalY=0 NormalZ=1 AngleXU=0 Radius=4.65
  constraints (2):
    c: Coincident(g0,g-1)
    c: Radius(g0) = 4.65
FEATURE [Sketcher::SketchObject] Sketch036
  MapMode = 5
  Placement = pos=(0,0,2) rot=(1,0,0;3.14159rad)
  sketch-geometry (2):
    g0: ArcOfCircle CenterX=0 CenterY=0 CenterZ=0 NormalX=0 NormalY=0 NormalZ=1 AngleXU=0 Radius=3 StartAngle=2.19024 EndAngle=7.23453
    g1: LineSegment StartX=-1.74176 StartY=2.4426 StartZ=0 EndX=1.74176 EndY=2.4426 EndZ=0
  constraints (5):
    c: Coincident(g0,g-1)
    c: Coincident(g1,g0)
    c: Coincident(g1,g0)
    c: Horizontal(g1)
    c: Radius(g0) = 3
FEATURE [PartDesign::Body] Body006  label="Outer003"
  Group = -> [Sketch032,Sketch033,Sketch030,AdditiveLoft004,Sketch031,Pad006,Sketch034,Sketch035,Sketch036]
  Origin = -> Origin006
  Placement = pos=(-10,10,0) rot=(0,0,1;0rad)
  Tip = -> Pad006
FEATURE [Sketcher::SketchObject] Sketch051
  MapMode = 5
  Support = -> [XY_Plane012]
  sketch-geometry (1):
    g0: Circle CenterX=0 CenterY=0 CenterZ=0 NormalX=0 NormalY=0 NormalZ=1 AngleXU=0 Radius=2
  constraints (2):
    c: Coincident(g0,g-1)
    c: Diameter(g0) = 4
FEATURE [PartDesign::Pad] Pad021
  Direction = (1,1,1)
  Length = 40
  Length2 = 100
  Profile = -> Sketch051
  Type = 0
FEATURE [PartDesign::Pad] Pad022
  BaseFeature = -> Pad021
  Direction = (1,1,1)
  Length = 4
  Length2 = 100
  Profile = -> Pad021 [Face2]
  Type = 0
FEATURE [PartDesign::Fillet] Fillet007
  Base = -> Pad022 [Edge5]
  BaseFeature = -> Pad022
  Radius = 1
  SupportTransform = false
FEATURE [Sketcher::SketchObject] Sketch052
  MapMode = 5
  Placement = pos=(0,0,0) rot=(0,1,0;3.14159rad)
  Support = -> [XY_Plane017]
  sketch-geometry (3):
    g0: ArcOfCircle CenterX=-8 CenterY=0 CenterZ=0 NormalX=0 NormalY=0 NormalZ=1 AngleXU=0 Radius=8.5 StartAngle=2.35619 EndAngle=3.92699
    g1: LineSegment [constr] StartX=-14.0104 StartY=6.01041 StartZ=0 EndX=-8 EndY=0 EndZ=0
    g2: LineSegment [constr] StartX=-8 StartY=0 StartZ=0 EndX=-14.0104 EndY=-6.01041 EndZ=0
  constraints (9):
    c: PointOnObject(g0,g-1)
    c: Coincident(g1,g0)
    c: Coincident(g1,g0)
    c: Coincident(g2,g0)
    c: Coincident(g2,g0)
    c: Angle(g-1,g1) = 2.35619
    c: Angle(g2,g-1) = 2.35619
    c: DistanceX(g0,g-1) = 8
    c: Radius(g0) = 8.5
FEATURE [Sketcher::SketchObject] Sketch053
  MapMode = 5
  Placement = pos=(0,0,0) rot=(1,0,0;1.5708rad)
  Support = -> [XZ_Plane017]
  sketch-geometry (1):
    g0: Circle CenterX=16.5 CenterY=0 CenterZ=0 NormalX=0 NormalY=0 NormalZ=1 AngleXU=0 Radius=1.25
  constraints (3):
    c: PointOnObject(g0,g-1)
    c: Diameter(g0) = 2.5
    c: DistanceX(g-1,g0) = 16.5
FEATURE [PartDesign::AdditivePipe] AdditivePipe
  AuxilleryCurvelinear = true
  AuxillerySpineTangent = false
  Binormal = (0,0,0)
  Mode = 0
  Placement = pos=(0,0,0) rot=(1,0,0;1.5708rad)
  Profile = -> Sketch053
  Spine = -> Sketch052 [Edge1]
  SpineTangent = false
  Transformation = 0
  Transition = 0
FEATURE [PartDesign::Chamfer] Chamfer005
  Angle = 45
  Base = -> AdditivePipe [Edge1]
  BaseFeature = -> AdditivePipe
  ChamferType = 1
  FlipDirection = false
  Placement = pos=(0,0,0) rot=(1,0,0;1.5708rad)
  Size = 1
  Size2 = 2
  SupportTransform = false
FEATURE [PartDesign::Chamfer] Chamfer006
  Angle = 45
  Base = -> Chamfer005 [Edge5]
  BaseFeature = -> Chamfer005
  ChamferType = 1
  FlipDirection = false
  Placement = pos=(0,0,0) rot=(1,0,0;1.5708rad)
  Size = 2
  Size2 = 1
  SupportTransform = false
FEATURE [Sketcher::SketchObject] Sketch054
  MapMode = 5
  Placement = pos=(0,0,0) rot=(0.57735,0.57735,0.57735;2.0944rad)
  Support = -> [YZ_Plane017]
  sketch-geometry (1):
    g0: Circle CenterX=0.00048 CenterY=0.002886 CenterZ=0 NormalX=0 NormalY=0 NormalZ=1 AngleXU=0 Radius=1.5
  constraints (1):
    c: Diameter(g0) = 3
FEATURE [PartDesign::Boolean] Boolean
  BaseFeature = -> Pad002
  Group = -> [Body,Body004,Body006,Body005]
  Type = 1
FEATURE [PartDesign::Pad] Pad023
  BaseFeature = -> Chamfer006
  Direction = (1,1,1)
  Length = 20
  Length2 = 100
  Placement = pos=(0,0,0) rot=(1,0,0;1.5708rad)
  Profile = -> Sketch054
  Type = 0
FEATURE [PartDesign::Fillet] Fillet
  Base = -> Pad023 [Edge12,Edge5,Edge11]
  BaseFeature = -> Pad023
  Placement = pos=(0,0,0) rot=(1,0,0;1.5708rad)
  Radius = 1
  SupportTransform = false
FEATURE [PartDesign::Body] Body017  label="runner"
  Group = -> [Sketch052,Sketch053,AdditivePipe,Chamfer005,Chamfer006,Sketch054,Pad023,Fillet]
  Origin = -> Origin017
  Tip = -> Fillet
FEATURE [PartDesign::FeatureBase] Clone
  BaseFeature = -> Body017
FEATURE [PartDesign::Body] Body018
  Group = -> [Clone]
  Origin = -> Origin018
  Placement = pos=(0,0,0) rot=(0,0,1;1.5708rad)
  Tip = -> Clone
FEATURE [PartDesign::FeatureBase] Clone001
  BaseFeature = -> Body017
FEATURE [PartDesign::Body] Body019
  Group = -> [Clone001]
  Origin = -> Origin019
  Placement = pos=(0,0,0) rot=(0,0,1;3.14159rad)
  Tip = -> Clone001
FEATURE [PartDesign::FeatureBase] Clone002
  BaseFeature = -> Body017
FEATURE [PartDesign::Body] Body020
  Group = -> [Clone002]
  Origin = -> Origin020
  Placement = pos=(0,0,0) rot=(0,0,1;4.71239rad)
  Tip = -> Clone002
FEATURE [PartDesign::Boolean] Boolean001
  BaseFeature = -> Fillet007
  Group = -> [Body017,Body018,Body019,Body020]
  Type = 0
FEATURE [PartDesign::Body] Body012  label="runner_main"
  Group = -> [Sketch051,Pad021,Pad022,Fillet007,Boolean001]
  Origin = -> Origin012
  Tip = -> Boolean001
FEATURE [Sketcher::SketchObject] Sketch055
  MapMode = 5
  Placement = pos=(0,0,0) rot=(1,0,0;1.5708rad)
  Support = -> [XZ_Plane021]
  sketch-geometry (7):
    g0: LineSegment StartX=-6 StartY=0 StartZ=0 EndX=-5.8 EndY=0 EndZ=0
    g1: LineSegment StartX=-5.8 StartY=0 StartZ=0 EndX=-4.5 EndY=15 EndZ=0
    g2: LineSegment StartX=-6 StartY=-5 StartZ=0 EndX=-6 EndY=0 EndZ=0
    g3: LineSegment [constr] StartX=-4.5 StartY=15 StartZ=0 EndX=0 EndY=0 EndZ=0
    g4: LineSegment StartX=-6 StartY=-5 StartZ=0 EndX=0 EndY=-5 EndZ=0
    g5: LineSegment StartX=0 StartY=-5 StartZ=0 EndX=0 EndY=15 EndZ=0
    g6: LineSegment StartX=0 StartY=15 StartZ=0 EndX=-4.5 EndY=15 EndZ=0
  constraints (20):
    c: PointOnObject(g0,g-1)
    c: Coincident(g0,g1)
    c: Coincident(g2,g0)
    c: PointOnObject(g0,g-1)
    c: Coincident(g1,g3)
    c: Coincident(g3,g-1)
    c: Vertical(g2)
    c: DistanceY(g2,g2) = 5
    c: DistanceY(g0,g1) = 15
    c: Coincident(g2,g4)
    c: PointOnObject(g4,g-2)
    c: Horizontal(g4)
    c: Coincident(g4,g5)
    c: PointOnObject(g5,g-2)
    c: Coincident(g5,g6)
    c: Coincident(g6,g1)
    c: Horizontal(g6)
    c: DistanceX(g4,g4) = 6
    c: DistanceX(g6,g6) = 4.5
    c: DistanceX(g0,g-1) = 5.8
FEATURE [PartDesign::Revolution] Revolution
  Angle = 360
  Axis = (0,2e-16,1)
  Base = (0,0,0)
  Placement = pos=(0,0,0) rot=(1,0,0;1.5708rad)
  Profile = -> Sketch055
  ReferenceAxis = -> Sketch055 [V_Axis]
FEATURE [PartDesign::Boolean] Boolean002
  BaseFeature = -> Revolution
  Group = -> [Body003]
  Type = 1
FEATURE [PartDesign::Body] Body021  label="Coreshape"
  Group = -> [Sketch055,Revolution,Boolean002]
  Origin = -> Origin021
  Placement = pos=(-10,-10,0) rot=(0,0,1;0rad)
  Tip = -> Boolean002
FEATURE [Sketcher::SketchObject] Sketch056
  MapMode = 5
  Support = -> [XY_Plane022]
  sketch-geometry (5):
    g0: LineSegment StartX=25 StartY=25 StartZ=0 EndX=-25 EndY=25 EndZ=0
    g1: LineSegment StartX=-25 StartY=25 StartZ=0 EndX=-25 EndY=-25 EndZ=0
    g2: LineSegment StartX=-25 StartY=-25 StartZ=0 EndX=25 EndY=-25 EndZ=0
    g3: LineSegment StartX=25 StartY=-25 StartZ=0 EndX=25 EndY=25 EndZ=0
    g4: Circle [constr] CenterX=0 CenterY=0 CenterZ=0 NormalX=0 NormalY=0 NormalZ=1 AngleXU=0 Radius=35.3553
  constraints (14):
    c: Coincident(g0,g1)
    c: Coincident(g1,g2)
    c: Coincident(g2,g3)
    c: Coincident(g3,g0)
    c: Equal(g0,g1)
    c: Equal(g0,g2)
    c: Equal(g0,g3)
    c: PointOnObject(g0,g4)
    c: PointOnObject(g1,g4)
    c: PointOnObject(g2,g4)
    c: PointOnObject(g3,g4)
    c: Coincident(g4,g-1)
    c: Horizontal(g0)
    c: DistanceX(g0,g0) = 50
FEATURE [PartDesign::Pad] Pad024
  Direction = (1,1,1)
  Length = 10
  Length2 = 100
  Profile = -> Sketch056
  Reversed = true
  Type = 0
FEATURE [PartDesign::FeatureBase] Clone003
  BaseFeature = -> Body021
FEATURE [PartDesign::Body] Body023
  Group = -> [Clone003]
  Origin = -> Origin023
  Placement = pos=(10,10,0) rot=(0,0,1;0rad)
  Tip = -> Clone003
FEATURE [PartDesign::FeatureBase] Clone004
  BaseFeature = -> Body021
FEATURE [PartDesign::Body] Body024
  Group = -> [Clone004]
  Origin = -> Origin024
  Placement = pos=(10,-10,0) rot=(0,0,1;0rad)
  Tip = -> Clone004
FEATURE [PartDesign::FeatureBase] Clone005
  BaseFeature = -> Body021
FEATURE [PartDesign::Body] Body025
  Group = -> [Clone005]
  Origin = -> Origin025
  Placement = pos=(-10,10,0) rot=(0,0,1;0rad)
  Tip = -> Clone005
FEATURE [PartDesign::Boolean] Boolean003
  BaseFeature = -> Pad024
  Group = -> [Body021,Body023,Body024,Body025]
  Refine = true
  Type = 0
FEATURE [PartDesign::FeatureBase] Clone006
  BaseFeature = -> Body012
FEATURE [PartDesign::Body] Body026  label="runner_main_core"
  Group = -> [Clone006]
  Origin = -> Origin026
  Tip = -> Clone006
FEATURE [PartDesign::Boolean] Boolean004
  BaseFeature = -> Boolean003
  Group = -> [Body026]
  Type = 1
FEATURE [PartDesign::Boolean] Boolean005
  BaseFeature = -> Boolean
  Group = -> [Body012]
  Type = 1
FEATURE [Sketcher::SketchObject] Sketch057
  MapMode = 5
  Placement = pos=(0,0,0) rot=(1,0,0;3.14159rad)
  Support = -> [Boolean005]
  sketch-geometry (9):
    g0: LineSegment [constr] StartX=-19 StartY=19 StartZ=0 EndX=-19 EndY=-19 EndZ=0
    g1: LineSegment [constr] StartX=-19 StartY=-19 StartZ=0 EndX=19 EndY=-19 EndZ=0
    g2: LineSegment [constr] StartX=19 StartY=-19 StartZ=0 EndX=19 EndY=19 EndZ=0
    g3: LineSegment [constr] StartX=19 StartY=19 StartZ=0 EndX=-19 EndY=19 EndZ=0
    g4: Circle [constr] CenterX=0 CenterY=0 CenterZ=0 NormalX=0 NormalY=0 NormalZ=1 AngleXU=0 Radius=26.8701
    g5: Circle CenterX=19 CenterY=19 CenterZ=0 NormalX=0 NormalY=0 NormalZ=1 AngleXU=0 Radius=3.6
    g6: Circle CenterX=19 CenterY=-19 CenterZ=0 NormalX=0 NormalY=0 NormalZ=1 AngleXU=0 Radius=3.6
    g7: Circle CenterX=-19 CenterY=-19 CenterZ=0 NormalX=0 NormalY=0 NormalZ=1 AngleXU=0 Radius=3.6
    g8: Circle CenterX=-19 CenterY=19 CenterZ=0 NormalX=0 NormalY=0 NormalZ=1 AngleXU=0 Radius=3.6
  constraints (22):
    c: Coincident(g0,g1)
    c: Coincident(g1,g2)
    c: Coincident(g2,g3)
    c: Coincident(g3,g0)
    c: Equal(g0,g1)
    c: Equal(g0,g2)
    c: Equal(g0,g3)
    c: PointOnObject(g0,g4)
    c: PointOnObject(g1,g4)
    c: PointOnObject(g2,g4)
    c: PointOnObject(g3,g4)
    c: Coincident(g4,g-1)
    c: Horizontal(g3)
    c: DistanceX(g3,g3) = 38
    c: Coincident(g5,g2)
    c: Coincident(g6,g1)
    c: Coincident(g7,g0)
    c: Coincident(g8,g0)
    c: Diameter(g8) = 7.2
    c: Equal(g8,g5)
    c: Equal(g8,g6)
    c: Equal(g8,g7)
FEATURE [PartDesign::Pocket] Pocket
  BaseFeature = -> Boolean005
  Length = 5
  Length2 = 100
  Profile = -> Sketch057
  Type = 0
FEATURE [Sketcher::SketchObject] Sketch058
  MapMode = 5
  Support = -> [Boolean004]
  sketch-geometry (9):
    g0: LineSegment [constr] StartX=19 StartY=19 StartZ=0 EndX=-19 EndY=19 EndZ=0
    g1: LineSegment [constr] StartX=-19 StartY=19 StartZ=0 EndX=-19 EndY=-19 EndZ=0
    g2: LineSegment [constr] StartX=-19 StartY=-19 StartZ=0 EndX=19 EndY=-19 EndZ=0
    g3: LineSegment [constr] StartX=19 StartY=-19 StartZ=0 EndX=19 EndY=19 EndZ=0
    g4: Circle [constr] CenterX=0 CenterY=0 CenterZ=0 NormalX=0 NormalY=0 NormalZ=1 AngleXU=0 Radius=26.8701
    g5: Circle CenterX=19 CenterY=19 CenterZ=0 NormalX=0 NormalY=0 NormalZ=1 AngleXU=0 Radius=3.5
    g6: Circle CenterX=-19 CenterY=19 CenterZ=0 NormalX=0 NormalY=0 NormalZ=1 AngleXU=0 Radius=3.5
    g7: Circle CenterX=-19 CenterY=-19 CenterZ=0 NormalX=0 NormalY=0 NormalZ=1 AngleXU=0 Radius=3.5
    g8: Circle CenterX=19 CenterY=-19 CenterZ=0 NormalX=0 NormalY=0 NormalZ=1 AngleXU=0 Radius=3.5
  constraints (22):
    c: Coincident(g0,g1)
    c: Coincident(g1,g2)
    c: Coincident(g2,g3)
    c: Coincident(g3,g0)
    c: Equal(g0,g1)
    c: Equal(g0,g2)
    c: Equal(g0,g3)
    c: PointOnObject(g0,g4)
    c: PointOnObject(g1,g4)
    c: PointOnObject(g2,g4)
    c: PointOnObject(g3,g4)
    c: Coincident(g4,g-1)
    c: Horizontal(g0)
    c: DistanceX(g0,g0) = 38
    c: Coincident(g5,g0)
    c: Coincident(g6,g0)
    c: Coincident(g7,g1)
    c: Coincident(g8,g2)
    c: Diameter(g8) = 7
    c: Equal(g8,g5)
    c: Equal(g8,g6)
    c: Equal(g8,g7)
FEATURE [PartDesign::Pad] Pad025
  BaseFeature = -> Boolean004
  Direction = (1,1,1)
  Length = 5
  Length2 = 100
  Profile = -> Sketch058
  Type = 0
FEATURE [PartDesign::Draft] Draft
  Angle = 5
  Base = -> Pad025 [Face56,Face7,Face58,Face9]
  BaseFeature = -> Pad025
  SupportTransform = false
FEATURE [PartDesign::Draft] Draft001
  Angle = 5
  Base = -> Pocket [Face106,Face7,Face8,Face105]
  BaseFeature = -> Pocket
  SupportTransform = false
FEATURE [PartDesign::Chamfer] Chamfer
  Angle = 45
  Base = -> Draft001 [Edge8,Edge2,Edge1,Edge5,Edge112,Edge7,Edge10,Edge4]
  BaseFeature = -> Draft001
  ChamferType = 0
  FlipDirection = false
  Size = 3
  Size2 = 1
  SupportTransform = false
FEATURE [PartDesign::Body] Body002  label="Base"
  Group = -> [Sketch008,Pad002,Boolean,Boolean005,Sketch057,Pocket,Draft001,Chamfer]
  Origin = -> Origin002
  Tip = -> Chamfer
FEATURE [PartDesign::Chamfer] Chamfer007
  Angle = 45
  Base = -> Draft [Edge4,Edge7,Edge1,Edge2,Edge8,Edge10,Edge104,Edge5]
  BaseFeature = -> Draft
  ChamferType = 0
  FlipDirection = false
  Size = 3
  Size2 = 1
  SupportTransform = false
FEATURE [PartDesign::Body] Body022  label="Core"
  Group = -> [Sketch056,Pad024,Boolean003,Boolean004,Sketch058,Pad025,Draft,Chamfer007]
  Origin = -> Origin022
  Tip = -> Chamfer007
